FCSTD DOCUMENT  (FreeCAD 1.0RUnknown)
Label: wardrobe_jan
License: All rights reserved
LicenseURL: https://en.wikipedia.org/wiki/All_rights_reserved
objects: App::Link×45, App::FeaturePython×9, Measure::MeasureDistance×9, Assembly::AssemblyLink×5, Assembly::JointGroup×1, Assembly::AssemblyObject×1, App::DocumentObjectGroup×1
EXTERNAL_REF file=room_corner_chimney_left.FCStd obj=Body010
EXTERNAL_REF file=subassemblies/wardrobe_corpus00_jan.FCStd obj=Assembly
EXTERNAL_REF file=subassemblies/wardrobe_corpus00_jan.FCStd obj=wardrobe_base_jan
EXTERNAL_REF file=subassemblies/wardrobe_corpus00_jan.FCStd obj=wardrobe_right_jan_corpus00
EXTERNAL_REF file=subassemblies/wardrobe_corpus00_jan.FCStd obj=wardrobe_left_jan_corpus00
EXTERNAL_REF file=subassemblies/wardrobe_corpus00_jan.FCStd obj=wardrobe_top_jan
EXTERNAL_REF file=subassemblies/wardrobe_corpus00_jan.FCStd obj=wardrobe_backplate_jan_corpus00
EXTERNAL_REF file=subassemblies/wardrobe_corpus01_jan.FCStd obj=Assembly
EXTERNAL_REF file=subassemblies/wardrobe_corpus01_jan.FCStd obj=wardrobe_base_jan
EXTERNAL_REF file=subassemblies/wardrobe_corpus01_jan.FCStd obj=wardrobe_right_jan_corpus00
EXTERNAL_REF file=subassemblies/wardrobe_corpus01_jan.FCStd obj=wardrobe_left_jan_corpus00
EXTERNAL_REF file=subassemblies/wardrobe_corpus01_jan.FCStd obj=wardrobe_top_jan
EXTERNAL_REF file=subassemblies/wardrobe_corpus01_jan.FCStd obj=wardrobe_backplate_jan_corpus00
EXTERNAL_REF file=subassemblies/wardrobe_corpus02_jan.FCStd obj=Assembly
EXTERNAL_REF file=subassemblies/wardrobe_corpus02_jan.FCStd obj=wardrobe_base_jan
EXTERNAL_REF file=subassemblies/wardrobe_corpus02_jan.FCStd obj=wardrobe_right_jan_corpus00
EXTERNAL_REF file=subassemblies/wardrobe_corpus02_jan.FCStd obj=wardrobe_left_jan_corpus00
EXTERNAL_REF file=subassemblies/wardrobe_corpus02_jan.FCStd obj=wardrobe_top_jan
EXTERNAL_REF file=subassemblies/wardrobe_corpus02_jan.FCStd obj=wardrobe_backplate_jan_corpus00
EXTERNAL_REF file=subassemblies/wardrobe_corpus00_jan.FCStd obj=hettich_level_adjustment
EXTERNAL_REF file=subassemblies/wardrobe_corpus00_jan.FCStd obj=hettich_level_adjustment001
EXTERNAL_REF file=subassemblies/wardrobe_corpus00_jan.FCStd obj=hettich_level_adjustment002
EXTERNAL_REF file=subassemblies/wardrobe_corpus00_jan.FCStd obj=hettich_level_adjustment003
EXTERNAL_REF file=subassemblies/wardrobe_corpus01_jan.FCStd obj=hettich_level_adjustment
EXTERNAL_REF file=subassemblies/wardrobe_corpus01_jan.FCStd obj=hettich_level_adjustment001
EXTERNAL_REF file=subassemblies/wardrobe_corpus01_jan.FCStd obj=hettich_level_adjustment002
EXTERNAL_REF file=subassemblies/wardrobe_corpus01_jan.FCStd obj=hettich_level_adjustment003
EXTERNAL_REF file=subassemblies/wardrobe_corpus02_jan.FCStd obj=hettich_level_adjustment
EXTERNAL_REF file=subassemblies/wardrobe_corpus02_jan.FCStd obj=hettich_level_adjustment001
EXTERNAL_REF file=subassemblies/wardrobe_corpus02_jan.FCStd obj=hettich_level_adjustment002
EXTERNAL_REF file=subassemblies/wardrobe_corpus02_jan.FCStd obj=hettich_level_adjustment003
EXTERNAL_REF file=subassemblies/wardrobe_corpus00_jan.FCStd obj=wardrobe_door_corpus00_jan
EXTERNAL_REF file=subassemblies/wardrobe_corpus01_jan.FCStd obj=wardrobe_door_corpus01_jan
EXTERNAL_REF file=subassemblies/wardrobe_corpus02_jan.FCStd obj=wardrobe_door_corpus02_jan
EXTERNAL_REF file=subassemblies/wardrobe_drawer_jan.FCStd obj=Assembly
EXTERNAL_REF file=subassemblies/wardrobe_drawer_jan.FCStd obj=hettich_rail_550
EXTERNAL_REF file=subassemblies/wardrobe_drawer_jan.FCStd obj=hettich_rail_551
EXTERNAL_REF file=subassemblies/wardrobe_drawer_jan.FCStd obj=drawer_sides
EXTERNAL_REF file=subassemblies/wardrobe_drawer_jan.FCStd obj=drawer_sides001
EXTERNAL_REF file=subassemblies/wardrobe_drawer_jan.FCStd obj=drawer_back
EXTERNAL_REF file=subassemblies/wardrobe_drawer_jan.FCStd obj=drawer_bottom
EXTERNAL_REF file=subassemblies/wardrobe_drawer_jan.FCStd obj=drawer_front
EXTERNAL_REF file=subassemblies/wardrobe_corpus00_jan.FCStd obj=wardrobe_drawer_jan

FEATURE [App::Link] wall  label="wall001"
  LinkPlacement = pos=(267.099,327.988,3.33374) rot=(0,0,1;0rad)
  LinkedObject = -> <external room_corner_chimney_left.FCStd>#Body010
  Placement = pos=(267.099,327.988,3.33374) rot=(0,0,1;0rad)
FEATURE [App::FeaturePython] GroundedJoint  # Assembly grounded joint (typed FeaturePython)
  ObjectToGround = -> wall
  Placement = pos=(267.099,327.988,3.33374) rot=(0,0,1;0rad)
FEATURE [App::Link] wardrobe_base_jan
  LinkedObject = -> <external subassemblies/wardrobe_corpus00_jan.FCStd>#wardrobe_base_jan
FEATURE [App::Link] wardrobe_right_jan_corpus00  label="wardrobe_right_corpus00_jan"
  LinkPlacement = pos=(251,2.07e-13,1022.5) rot=(0,0,1;0rad)
  LinkedObject = -> <external subassemblies/wardrobe_corpus00_jan.FCStd>#wardrobe_right_jan_corpus00
  Placement = pos=(251,2.07e-13,1022.5) rot=(0,0,1;0rad)
FEATURE [App::Link] wardrobe_left_jan_corpus00  label="wardrobe_left_corpus00_jan"
  LinkPlacement = pos=(-270,2.1e-13,1022.5) rot=(0,0,1;0rad)
  LinkedObject = -> <external subassemblies/wardrobe_corpus00_jan.FCStd>#wardrobe_left_jan_corpus00
  Placement = pos=(-270,2.1e-13,1022.5) rot=(0,0,1;0rad)
FEATURE [App::Link] wardrobe_top_jan
  LinkPlacement = pos=(-6.835e-13,3.905e-13,2026) rot=(0,0,1;0rad)
  LinkedObject = -> <external subassemblies/wardrobe_corpus00_jan.FCStd>#wardrobe_top_jan
  Placement = pos=(-6.835e-13,3.905e-13,2026) rot=(0,0,1;0rad)
FEATURE [App::Link] wardrobe_backplate_jan_corpus00  label="wardrobe_backplate_corpus00_jan"
  LinkPlacement = pos=(-3e-15,300,1022.5) rot=(0,0,1;3.14159rad)
  LinkedObject = -> <external subassemblies/wardrobe_corpus00_jan.FCStd>#wardrobe_backplate_jan_corpus00
  Placement = pos=(-3e-15,300,1022.5) rot=(0,0,1;3.14159rad)
FEATURE [App::Link] wardrobe_base_jan001
  LinkedObject = -> <external subassemblies/wardrobe_corpus01_jan.FCStd>#wardrobe_base_jan
FEATURE [App::Link] wardrobe_right_jan_corpus001  label="wardrobe_right_corpus01_jan"
  LinkPlacement = pos=(251,1.01e-13,707.5) rot=(0,0,1;0rad)
  LinkedObject = -> <external subassemblies/wardrobe_corpus01_jan.FCStd>#wardrobe_right_jan_corpus00
  Placement = pos=(251,1.01e-13,707.5) rot=(0,0,1;0rad)
FEATURE [App::Link] wardrobe_left_jan_corpus001  label="wardrobe_left_corpus01_jan"
  LinkPlacement = pos=(-270,9.63e-14,707.5) rot=(0,0,1;0rad)
  LinkedObject = -> <external subassemblies/wardrobe_corpus01_jan.FCStd>#wardrobe_left_jan_corpus00
  Placement = pos=(-270,9.63e-14,707.5) rot=(0,0,1;0rad)
FEATURE [App::Link] wardrobe_top_jan001
  LinkPlacement = pos=(-4.699e-13,1.441e-13,1396) rot=(0,0,1;0rad)
  LinkedObject = -> <external subassemblies/wardrobe_corpus01_jan.FCStd>#wardrobe_top_jan
  Placement = pos=(-4.699e-13,1.441e-13,1396) rot=(0,0,1;0rad)
FEATURE [App::Link] wardrobe_backplate_jan_corpus001  label="wardrobe_backplate_corpus01_jan"
  LinkPlacement = pos=(-3e-15,300,707.5) rot=(0,0,1;3.14159rad)
  LinkedObject = -> <external subassemblies/wardrobe_corpus01_jan.FCStd>#wardrobe_backplate_jan_corpus00
  Placement = pos=(-3e-15,300,707.5) rot=(0,0,1;3.14159rad)
FEATURE [App::Link] wardrobe_base_jan002
  LinkedObject = -> <external subassemblies/wardrobe_corpus02_jan.FCStd>#wardrobe_base_jan
FEATURE [App::Link] wardrobe_right_jan_corpus002  label="wardrobe_right_corpus02_jan"
  LinkPlacement = pos=(251,-5.11e-14,390) rot=(0,0,1;0rad)
  LinkedObject = -> <external subassemblies/wardrobe_corpus02_jan.FCStd>#wardrobe_right_jan_corpus00
  Placement = pos=(251,-5.11e-14,390) rot=(0,0,1;0rad)
FEATURE [App::Link] wardrobe_left_jan_corpus002  label="wardrobe_left_corpus02_jan"
  LinkPlacement = pos=(-270,9.63e-14,390) rot=(0,0,1;0rad)
  LinkedObject = -> <external subassemblies/wardrobe_corpus02_jan.FCStd>#wardrobe_left_jan_corpus00
  Placement = pos=(-270,9.63e-14,390) rot=(0,0,1;0rad)
FEATURE [App::Link] wardrobe_top_jan002
  LinkPlacement = pos=(-2.095e-13,-1.636e-13,761) rot=(0,0,1;0rad)
  LinkedObject = -> <external subassemblies/wardrobe_corpus02_jan.FCStd>#wardrobe_top_jan
  Placement = pos=(-2.095e-13,-1.636e-13,761) rot=(0,0,1;0rad)
FEATURE [App::Link] wardrobe_backplate_jan_corpus002  label="wardrobe_backplate_corpus02_jan"
  LinkPlacement = pos=(-3e-15,300,390) rot=(0,0,1;3.14159rad)
  LinkedObject = -> <external subassemblies/wardrobe_corpus02_jan.FCStd>#wardrobe_backplate_jan_corpus00
  Placement = pos=(-3e-15,300,390) rot=(0,0,1;3.14159rad)
FEATURE [App::FeaturePython] Joint  label="Parallel"  # Assembly joint (typed FeaturePython)
  Activated = true
  AngleMax = 0
  AngleMin = 0
  Detach1 = false
  Detach2 = false
  Distance = 0
  Distance2 = 0
  EnableAngleMax = false
  EnableAngleMin = false
  EnableLengthMax = false
  EnableLengthMin = false
  JointType = 6 (Parallel)
  LengthMax = 0
  LengthMin = 0
  Placement1 = pos=(-1.2e-15,-19,0) rot=(-0.57735,-0.57735,-0.57735;2.0944rad)
  Placement2 = pos=(-777.564,-2.274e-13,902.667) rot=(-0.57735,-0.57735,-0.57735;2.0944rad)
  Reference1 = -> Assembly [wardrobe_corpus00_jan.wardrobe_backplate_jan_corpus00.Face6,wardrobe_corpus00_jan.wardrobe_backplate_jan_corpus00.Face6]
  Reference2 = -> Assembly [wall.Face7,wall.Face7]
FEATURE [App::FeaturePython] Joint001  label="Parallel001"  # Assembly joint (typed FeaturePython)
  Activated = true
  AngleMax = 0
  AngleMin = 0
  Detach1 = false
  Detach2 = false
  Distance = 0
  Distance2 = 0
  EnableAngleMax = false
  EnableAngleMin = false
  EnableLengthMax = false
  EnableLengthMin = false
  JointType = 6 (Parallel)
  LengthMax = 0
  LengthMin = 0
  Placement1 = pos=(19,1.005e-13,0) rot=(0.707107,0,0.707107;3.14159rad)
  Placement2 = pos=(0,-335,1240) rot=(0,-1,0;1.5708rad)
  Reference1 = -> Assembly [wardrobe_corpus00_jan.wardrobe_right_jan_corpus00.Face6,wardrobe_corpus00_jan.wardrobe_right_jan_corpus00.Face6]
  Reference2 = -> Assembly [wall.Face6,wall.Face6]
FEATURE [App::FeaturePython] Joint002  label="Parallel002"  # Assembly joint (typed FeaturePython)
  Activated = true
  AngleMax = 0
  AngleMin = 0
  Detach1 = false
  Detach2 = false
  Distance = 0
  Distance2 = 0
  EnableAngleMax = false
  EnableAngleMin = false
  EnableLengthMax = false
  EnableLengthMin = false
  JointType = 6 (Parallel)
  LengthMax = 0
  LengthMin = 0
  Placement1 = pos=(-1.3e-15,0,0) rot=(0,0,1;0rad)
  Placement2 = pos=(-1080,-335,7.37e-14) rot=(0,1,0;3.14159rad)
  Reference1 = -> Assembly [wardrobe_corpus00_jan.wardrobe_base_jan.Face5,wardrobe_corpus00_jan.wardrobe_base_jan.Face5]
  Reference2 = -> Assembly [wall.Face2,wall.Face2]
FEATURE [App::FeaturePython] Joint003  label="Abstand"  # Assembly joint (typed FeaturePython)
  Activated = true
  AngleMax = 0
  AngleMin = 0
  Detach1 = false
  Detach2 = false
  Distance = -30
  Distance2 = 0
  EnableAngleMax = false
  EnableAngleMin = false
  EnableLengthMax = false
  EnableLengthMin = false
  JointType = 5 (Distance)
  LengthMax = 0
  LengthMin = 0
  Placement1 = pos=(-1.3e-15,0,0) rot=(0,0,1;0rad)
  Placement2 = pos=(-1080,-335,7.37e-14) rot=(0,1,0;3.14159rad)
  Reference1 = -> Assembly [wardrobe_corpus00_jan.wardrobe_base_jan.Face5,wardrobe_corpus00_jan.wardrobe_base_jan.Face5]
  Reference2 = -> Assembly [wall.Face2,wall.Face2]
FEATURE [App::FeaturePython] Joint004  label="Abstand001"  # Assembly joint (typed FeaturePython)
  Activated = true
  AngleMax = 0
  AngleMin = 0
  Detach1 = false
  Detach2 = false
  Distance = 10
  Distance2 = 0
  EnableAngleMax = false
  EnableAngleMin = false
  EnableLengthMax = false
  EnableLengthMin = false
  JointType = 5 (Distance)
  LengthMax = 0
  LengthMin = 0
  Placement1 = pos=(19,1.005e-13,0) rot=(0.707107,0,0.707107;3.14159rad)
  Placement2 = pos=(0,-335,1240) rot=(0,-1,0;1.5708rad)
  Reference1 = -> Assembly [wardrobe_corpus00_jan.wardrobe_right_jan_corpus00.Face6,wardrobe_corpus00_jan.wardrobe_right_jan_corpus00.Face6]
  Reference2 = -> Assembly [wall.Face6,wall.Face6]
FEATURE [App::FeaturePython] Joint005  label="Abstand002"  # Assembly joint (typed FeaturePython)
  Activated = true
  AngleMax = 0
  AngleMin = 0
  Detach1 = false
  Detach2 = false
  Distance = 5
  Distance2 = 0
  EnableAngleMax = false
  EnableAngleMin = false
  EnableLengthMax = false
  EnableLengthMin = false
  JointType = 5 (Distance)
  LengthMax = 0
  LengthMin = 0
  Placement1 = pos=(-1.2e-15,-19,0) rot=(-0.57735,-0.57735,-0.57735;2.0944rad)
  Placement2 = pos=(-777.564,-2.274e-13,902.667) rot=(-0.57735,-0.57735,-0.57735;2.0944rad)
  Reference1 = -> Assembly [wardrobe_corpus00_jan.wardrobe_backplate_jan_corpus00.Face6,wardrobe_corpus00_jan.wardrobe_backplate_jan_corpus00.Face6]
  Reference2 = -> Assembly [wall.Face7,wall.Vertex11]
FEATURE [App::FeaturePython] Joint006  label="StarrerVerbund"  # Assembly joint (typed FeaturePython)
  Activated = true
  AngleMax = 0
  AngleMin = 0
  Detach1 = false
  Detach2 = false
  Distance = 0
  Distance2 = 0
  EnableAngleMax = false
  EnableAngleMin = false
  EnableLengthMax = false
  EnableLengthMin = false
  JointType = 0 (Fixed)
  LengthMax = 0
  LengthMin = 0
  Offset2 = pos=(0,0,0) rot=(0,0,1;3.14159rad)
  Placement1 = pos=(270,0,0) rot=(0.57735,0.57735,0.57735;4.18879rad)
  Placement2 = pos=(-270,0,0) rot=(-0.57735,0.57735,-0.57735;4.18879rad)
  Reference1 = -> Assembly [wardrobe_corpus01_jan.wardrobe_base_jan001.Edge6,wardrobe_corpus01_jan.wardrobe_base_jan001.Edge6]
  Reference2 = -> Assembly [wardrobe_corpus00_jan.wardrobe_base_jan.Edge11,wardrobe_corpus00_jan.wardrobe_base_jan.Edge11]
FEATURE [App::FeaturePython] Joint007  label="StarrerVerbund001"  # Assembly joint (typed FeaturePython)
  Activated = true
  AngleMax = 0
  AngleMin = 0
  Detach1 = false
  Detach2 = false
  Distance = 0
  Distance2 = 0
  EnableAngleMax = false
  EnableAngleMin = false
  EnableLengthMax = false
  EnableLengthMin = false
  JointType = 0 (Fixed)
  LengthMax = 0
  LengthMin = 0
  Offset2 = pos=(0,0,0) rot=(0,0,1;3.14159rad)
  Placement1 = pos=(270,0,0) rot=(0.57735,0.57735,0.57735;4.18879rad)
  Placement2 = pos=(-270,0,0) rot=(-0.57735,0.57735,-0.57735;4.18879rad)
  Reference1 = -> Assembly [wardrobe_corpus02_jan.wardrobe_base_jan002.Edge6,wardrobe_corpus02_jan.wardrobe_base_jan002.Edge6]
  Reference2 = -> Assembly [wardrobe_corpus01_jan.wardrobe_base_jan001.Edge11,wardrobe_corpus01_jan.wardrobe_base_jan001.Edge11]
FEATURE [Assembly::JointGroup] Joints
  Group = -> [GroundedJoint,Joint,Joint001,Joint002,Joint003,Joint004,Joint005,Joint006,Joint007]
FEATURE [App::Link] hettich_level_adjustment  label="hettich-level-adjustment"
  LinkPlacement = pos=(-218.25,-240,-1.33e-14) rot=(0.707107,-0.707107,0;3.14159rad)
  LinkedObject = -> <external subassemblies/wardrobe_corpus00_jan.FCStd>#hettich_level_adjustment
  Placement = pos=(-218.25,-240,-1.33e-14) rot=(0.707107,-0.707107,0;3.14159rad)
FEATURE [App::Link] hettich_level_adjustment001  label="hettich-level-adjustment001"
  LinkPlacement = pos=(218.25,-240,-3.9e-15) rot=(0.707107,-0.707107,0;3.14159rad)
  LinkedObject = -> <external subassemblies/wardrobe_corpus00_jan.FCStd>#hettich_level_adjustment001
  Placement = pos=(218.25,-240,-3.9e-15) rot=(0.707107,-0.707107,0;3.14159rad)
FEATURE [App::Link] hettich_level_adjustment002  label="hettich-level-adjustment002"
  LinkPlacement = pos=(218.25,240,-1.33e-14) rot=(0.707107,-0.707107,0;3.14159rad)
  LinkedObject = -> <external subassemblies/wardrobe_corpus00_jan.FCStd>#hettich_level_adjustment002
  Placement = pos=(218.25,240,-1.33e-14) rot=(0.707107,-0.707107,0;3.14159rad)
FEATURE [App::Link] hettich_level_adjustment003  label="hettich-level-adjustment003"
  LinkPlacement = pos=(-218.25,240,1.33e-14) rot=(0.707107,0.707107,0;3.14159rad)
  LinkedObject = -> <external subassemblies/wardrobe_corpus00_jan.FCStd>#hettich_level_adjustment003
  Placement = pos=(-218.25,240,1.33e-14) rot=(0.707107,0.707107,0;3.14159rad)
FEATURE [App::Link] hettich_level_adjustment004  label="hettich-level-adjustment004"
  LinkPlacement = pos=(-218.25,-240,-1.33e-14) rot=(0.707107,0.707107,0;3.14159rad)
  LinkedObject = -> <external subassemblies/wardrobe_corpus01_jan.FCStd>#hettich_level_adjustment
  Placement = pos=(-218.25,-240,-1.33e-14) rot=(0.707107,0.707107,0;3.14159rad)
FEATURE [App::Link] hettich_level_adjustment005  label="hettich-level-adjustment005"
  LinkPlacement = pos=(218.25,-240,1.33e-14) rot=(0.707107,-0.707107,0;3.14159rad)
  LinkedObject = -> <external subassemblies/wardrobe_corpus01_jan.FCStd>#hettich_level_adjustment001
  Placement = pos=(218.25,-240,1.33e-14) rot=(0.707107,-0.707107,0;3.14159rad)
FEATURE [App::Link] hettich_level_adjustment006  label="hettich-level-adjustment006"
  LinkPlacement = pos=(218.25,240,-1.33e-14) rot=(0.707107,-0.707107,0;3.14159rad)
  LinkedObject = -> <external subassemblies/wardrobe_corpus01_jan.FCStd>#hettich_level_adjustment002
  Placement = pos=(218.25,240,-1.33e-14) rot=(0.707107,-0.707107,0;3.14159rad)
FEATURE [App::Link] hettich_level_adjustment007  label="hettich-level-adjustment007"
  LinkPlacement = pos=(-218.25,240,1.33e-14) rot=(0.707107,0.707107,0;3.14159rad)
  LinkedObject = -> <external subassemblies/wardrobe_corpus01_jan.FCStd>#hettich_level_adjustment003
  Placement = pos=(-218.25,240,1.33e-14) rot=(0.707107,0.707107,0;3.14159rad)
FEATURE [App::Link] hettich_level_adjustment008  label="hettich-level-adjustment008"
  LinkPlacement = pos=(-218.25,-240,-1.33e-14) rot=(0.707107,0.707107,0;3.14159rad)
  LinkedObject = -> <external subassemblies/wardrobe_corpus02_jan.FCStd>#hettich_level_adjustment
  Placement = pos=(-218.25,-240,-1.33e-14) rot=(0.707107,0.707107,0;3.14159rad)
FEATURE [App::Link] hettich_level_adjustment009  label="hettich-level-adjustment009"
  LinkPlacement = pos=(218.25,-240,-3.9e-15) rot=(-0.707107,0.707107,0;3.14159rad)
  LinkedObject = -> <external subassemblies/wardrobe_corpus02_jan.FCStd>#hettich_level_adjustment001
  Placement = pos=(218.25,-240,-3.9e-15) rot=(-0.707107,0.707107,0;3.14159rad)
FEATURE [App::Link] hettich_level_adjustment010  label="hettich-level-adjustment010"
  LinkPlacement = pos=(218.25,240,-1.97e-14) rot=(0.707107,-0.707107,0;3.14159rad)
  LinkedObject = -> <external subassemblies/wardrobe_corpus02_jan.FCStd>#hettich_level_adjustment002
  Placement = pos=(218.25,240,-1.97e-14) rot=(0.707107,-0.707107,0;3.14159rad)
FEATURE [App::Link] hettich_level_adjustment011  label="hettich-level-adjustment011"
  LinkPlacement = pos=(-218.25,240,1.33e-14) rot=(0.707107,0.707107,0;3.14159rad)
  LinkedObject = -> <external subassemblies/wardrobe_corpus02_jan.FCStd>#hettich_level_adjustment003
  Placement = pos=(-218.25,240,1.33e-14) rot=(0.707107,0.707107,0;3.14159rad)
FEATURE [App::Link] wardrobe_door_corpus00_jan
  LinkPlacement = pos=(270,-302,2.5) rot=(0.57735,0.57735,0.57735;2.0944rad)
  LinkedObject = -> <external subassemblies/wardrobe_corpus00_jan.FCStd>#wardrobe_door_corpus00_jan
  Placement = pos=(270,-302,2.5) rot=(0.57735,0.57735,0.57735;2.0944rad)
FEATURE [App::Link] wardrobe_door_corpus01_jan
  LinkPlacement = pos=(267.5,-300,-2.1e-15) rot=(1,0,0;1.5708rad)
  LinkedObject = -> <external subassemblies/wardrobe_corpus01_jan.FCStd>#wardrobe_door_corpus01_jan
  Placement = pos=(267.5,-300,-2.1e-15) rot=(1,0,0;1.5708rad)
FEATURE [Assembly::AssemblyLink] wardrobe_corpus01_jan
  Group = -> [wardrobe_base_jan001,wardrobe_right_jan_corpus001,wardrobe_left_jan_corpus001,wardrobe_top_jan001,wardrobe_backplate_jan_corpus001,hettich_level_adjustment004,hettich_level_adjustment005,hettich_level_adjustment006,hettich_level_adjustment007,wardrobe_door_corpus01_jan]
  LinkedObject = -> <external subassemblies/wardrobe_corpus01_jan.FCStd>#Assembly
  Origin = -> Origin014
  Placement = pos=(-552.901,13.9879,33.3337) rot=(0,0,1;0rad)
  Rigid = true
FEATURE [App::Link] wardrobe_door_corpus02_jan
  LinkPlacement = pos=(267.5,-300,2.1e-15) rot=(1,0,0;1.5708rad)
  LinkedObject = -> <external subassemblies/wardrobe_corpus02_jan.FCStd>#wardrobe_door_corpus02_jan
  Placement = pos=(267.5,-300,2.1e-15) rot=(1,0,0;1.5708rad)
FEATURE [Assembly::AssemblyLink] wardrobe_corpus02_jan
  Group = -> [wardrobe_base_jan002,wardrobe_right_jan_corpus002,wardrobe_left_jan_corpus002,wardrobe_top_jan002,wardrobe_backplate_jan_corpus002,hettich_level_adjustment008,hettich_level_adjustment009,hettich_level_adjustment010,hettich_level_adjustment011,wardrobe_door_corpus02_jan]
  LinkedObject = -> <external subassemblies/wardrobe_corpus02_jan.FCStd>#Assembly
  Origin = -> Origin015
  Placement = pos=(-1092.9,13.9879,33.3337) rot=(0,0,1;0rad)
  Rigid = true
FEATURE [App::Link] hettich_rail_550
  LinkPlacement = pos=(0,-8.67788e-07,0) rot=(0.57735,0.57735,0.57735;2.0944rad)
  LinkedObject = -> <external subassemblies/wardrobe_drawer_jan.FCStd>#hettich_rail_550
  Placement = pos=(0,-8.67788e-07,0) rot=(0.57735,0.57735,0.57735;2.0944rad)
FEATURE [App::Link] hettich_rail_551  label="hettich_rail_550_1"
  LinkPlacement = pos=(502,3.32992e-05,-3.4167e-05) rot=(0.57735,-0.57735,-0.57735;2.0944rad)
  LinkedObject = -> <external subassemblies/wardrobe_drawer_jan.FCStd>#hettich_rail_551
  Placement = pos=(502,3.32992e-05,-3.4167e-05) rot=(0.57735,-0.57735,-0.57735;2.0944rad)
FEATURE [App::Link] drawer_sides
  LinkPlacement = pos=(22,256,72.5) rot=(-0.340731,0.659269,0.659269;0rad)
  LinkedObject = -> <external subassemblies/wardrobe_drawer_jan.FCStd>#drawer_sides
  Placement = pos=(22,256,72.5) rot=(-0.340731,0.659269,0.659269;0rad)
FEATURE [App::Link] drawer_sides001
  LinkPlacement = pos=(480,-256,72.5) rot=(0,0,1;3.14159rad)
  LinkedObject = -> <external subassemblies/wardrobe_drawer_jan.FCStd>#drawer_sides001
  Placement = pos=(480,-256,72.5) rot=(0,0,1;3.14159rad)
FEATURE [App::Link] drawer_back
  LinkPlacement = pos=(489.5,265.5,80.75) rot=(0,0,-1;1.5708rad)
  LinkedObject = -> <external subassemblies/wardrobe_drawer_jan.FCStd>#drawer_back
  Placement = pos=(489.5,265.5,80.75) rot=(0,0,-1;1.5708rad)
FEATURE [App::Link] drawer_bottom
  LinkPlacement = pos=(251,5.75002,-2.50002) rot=(0,0,1;3.14159rad)
  LinkedObject = -> <external subassemblies/wardrobe_drawer_jan.FCStd>#drawer_bottom
  Placement = pos=(251,5.75002,-2.50002) rot=(0,0,1;3.14159rad)
FEATURE [App::Link] drawer_front
  LinkPlacement = pos=(12.5,-265.5,72.5) rot=(0,0,1;1.5708rad)
  LinkedObject = -> <external subassemblies/wardrobe_drawer_jan.FCStd>#drawer_front
  Placement = pos=(12.5,-265.5,72.5) rot=(0,0,1;1.5708rad)
FEATURE [Assembly::AssemblyLink] wardrobe_drawer_jan
  Group = -> [hettich_rail_550,hettich_rail_551,drawer_sides,drawer_sides001,drawer_back,drawer_bottom,drawer_front]
  LinkedObject = -> <external subassemblies/wardrobe_drawer_jan.FCStd>#Assembly
  Placement = pos=(-251,8.67788e-07,36.5) rot=(0.340731,-0.659269,-0.659269;0rad)
  Rigid = true
FEATURE [App::Link] hettich_rail_552
  LinkPlacement = pos=(0,-8.67788e-07,0) rot=(0.57735,0.57735,0.57735;2.0944rad)
  LinkedObject = -> <external subassemblies/wardrobe_drawer_jan.FCStd>#hettich_rail_550
  Placement = pos=(0,-8.67788e-07,0) rot=(0.57735,0.57735,0.57735;2.0944rad)
FEATURE [App::Link] hettich_rail_553  label="hettich_rail_550_002"
  LinkPlacement = pos=(502,3.32992e-05,-3.4167e-05) rot=(0.57735,-0.57735,-0.57735;2.0944rad)
  LinkedObject = -> <external subassemblies/wardrobe_drawer_jan.FCStd>#hettich_rail_551
  Placement = pos=(502,3.32992e-05,-3.4167e-05) rot=(0.57735,-0.57735,-0.57735;2.0944rad)
FEATURE [App::Link] drawer_sides002
  LinkPlacement = pos=(22,256,72.5) rot=(-0.340731,0.659269,0.659269;0rad)
  LinkedObject = -> <external subassemblies/wardrobe_drawer_jan.FCStd>#drawer_sides
  Placement = pos=(22,256,72.5) rot=(-0.340731,0.659269,0.659269;0rad)
FEATURE [App::Link] drawer_sides003
  LinkPlacement = pos=(480,-256,72.5) rot=(0,0,1;3.14159rad)
  LinkedObject = -> <external subassemblies/wardrobe_drawer_jan.FCStd>#drawer_sides001
  Placement = pos=(480,-256,72.5) rot=(0,0,1;3.14159rad)
FEATURE [App::Link] drawer_back001
  LinkPlacement = pos=(489.5,265.5,80.75) rot=(0,0,-1;1.5708rad)
  LinkedObject = -> <external subassemblies/wardrobe_drawer_jan.FCStd>#drawer_back
  Placement = pos=(489.5,265.5,80.75) rot=(0,0,-1;1.5708rad)
FEATURE [App::Link] drawer_bottom001
  LinkPlacement = pos=(251,5.75002,-2.50002) rot=(0,0,1;3.14159rad)
  LinkedObject = -> <external subassemblies/wardrobe_drawer_jan.FCStd>#drawer_bottom
  Placement = pos=(251,5.75002,-2.50002) rot=(0,0,1;3.14159rad)
FEATURE [App::Link] drawer_front001
  LinkPlacement = pos=(12.5,-265.5,72.5) rot=(0,0,1;1.5708rad)
  LinkedObject = -> <external subassemblies/wardrobe_drawer_jan.FCStd>#drawer_front
  Placement = pos=(12.5,-265.5,72.5) rot=(0,0,1;1.5708rad)
FEATURE [Assembly::AssemblyLink] wardrobe_drawer_jan001
  Group = -> [hettich_rail_552,hettich_rail_553,drawer_sides002,drawer_sides003,drawer_back001,drawer_bottom001,drawer_front001]
  LinkedObject = -> <external subassemblies/wardrobe_corpus00_jan.FCStd>#wardrobe_drawer_jan
  Placement = pos=(-251,8.67788e-07,56.5) rot=(0.340731,-0.659269,-0.659269;0rad)
  Rigid = true
FEATURE [Assembly::AssemblyLink] wardrobe_corpus00_jan
  Group = -> [wardrobe_base_jan,wardrobe_right_jan_corpus00,wardrobe_left_jan_corpus00,wardrobe_top_jan,wardrobe_backplate_jan_corpus00,hettich_level_adjustment,hettich_level_adjustment001,hettich_level_adjustment002,hettich_level_adjustment003,wardrobe_door_corpus00_jan,wardrobe_drawer_jan,wardrobe_drawer_jan001]
  LinkedObject = -> <external subassemblies/wardrobe_corpus00_jan.FCStd>#Assembly
  Origin = -> Origin
  Placement = pos=(-12.9011,13.9879,33.3337) rot=(0,0,1;0rad)
  Rigid = true
FEATURE [Assembly::AssemblyObject] Assembly
  Group = -> [Joints,wall,GroundedJoint,wardrobe_corpus00_jan,wardrobe_corpus01_jan,wardrobe_corpus02_jan,Joint,Joint001,Joint002,Joint003,Joint004,Joint005,Joint006,Joint007]
  Origin = -> Origin003
  Type = Assembly
FEATURE [Measure::MeasureDistance] Distance  label="Distance: 12,26 mm"
  Distance = 12.257
  DistanceX = 9.31778
  DistanceY = 0
  DistanceZ = 7.96321
  Element1 = -> Assembly [wardrobe_corpus00_jan.wardrobe_top_jan.Pad003.Edge12]
  Element2 = -> Assembly [wall.Pad.Face4]
  Position1 = (-282.901,326.988,2078.33)
  Position2 = (-292.219,326.988,2086.3)
FEATURE [Measure::MeasureDistance] Distance001  label="Distance001: 11,05 mm"
  Distance = 11.0514
  DistanceX = 8.40128
  DistanceY = 0
  DistanceZ = 7.17995
  Element1 = -> Assembly [wardrobe_corpus01_jan.wardrobe_top_jan001.Pad003.Edge12]
  Element2 = -> Assembly [wall.Pad.Face4]
  Position1 = (-822.901,326.988,1448.33)
  Position2 = (-831.302,326.988,1455.51)
FEATURE [Measure::MeasureDistance] Distance002  label="Distance002: 13,09 mm"
  Distance = 13.0942
  DistanceX = 9.95424
  DistanceY = 0
  DistanceZ = 8.50715
  Element1 = -> Assembly [wardrobe_corpus02_jan.wardrobe_top_jan002.Pad003.Edge12]
  Element2 = -> Assembly [wall.Pad.Face4]
  Position1 = (-1362.9,326.988,813.334)
  Position2 = (-1372.86,326.988,821.841)
FEATURE [Measure::MeasureDistance] Distance003  label="Distance003: 2075,00 mm"
  Distance = 2075
  DistanceX = 0
  DistanceY = 4.547e-13
  DistanceZ = 2075
  Element1 = -> Assembly [wardrobe_corpus00_jan.wardrobe_top_jan.Pad003.Face6]
  Element2 = -> Assembly [wall.Pad.Face2]
  Position1 = (-282.901,-273.012,2078.33)
  Position2 = (-282.901,-273.012,3.33374)
FEATURE [Measure::MeasureDistance] Distance004  label="Distance004: 1445,00 mm"
  Distance = 1445
  DistanceX = 0
  DistanceY = 3.411e-13
  DistanceZ = 1445
  Element1 = -> Assembly [wardrobe_corpus01_jan.wardrobe_top_jan001.Pad003.Face6]
  Element2 = -> Assembly [wall.Pad.Face2]
  Position1 = (-822.901,-273.012,1448.33)
  Position2 = (-822.901,-273.012,3.33374)
FEATURE [Measure::MeasureDistance] Distance005  label="Distance005: 810,00 mm"
  Distance = 810
  DistanceX = 0
  DistanceY = 1.705e-13
  DistanceZ = 810
  Element1 = -> Assembly [wardrobe_corpus02_jan.wardrobe_top_jan002.Pad003.Face6]
  Element2 = -> Assembly [wall.Pad.Face2]
  Position1 = (-1362.9,-273.012,813.334)
  Position2 = (-1362.9,-273.012,3.33374)
FEATURE [Measure::MeasureDistance] Distance006  label="Distance006: 540,00 mm"
  Distance = 540
  DistanceX = 540
  DistanceY = 0
  DistanceZ = 0
  Element1 = -> Assembly [wardrobe_corpus00_jan.wardrobe_left_jan_corpus00.Pad001.Face5]
  Element2 = -> Assembly [wardrobe_corpus00_jan.wardrobe_right_jan_corpus00.Pad002.Face6]
  Position1 = (-282.901,-273.012,52.3337)
  Position2 = (257.099,-273.012,52.3337)
FEATURE [Measure::MeasureDistance] Distance007  label="Distance007: 10,00 mm"
  Distance = 10
  DistanceX = 10
  DistanceY = 0
  DistanceZ = 0
  Element1 = -> Assembly [wardrobe_corpus00_jan.wardrobe_right_jan_corpus00.Pad002.Face6]
  Element2 = -> Assembly [wall.Pad.Face6]
  Position1 = (257.099,-273.012,52.3337)
  Position2 = (267.099,-273.012,52.3337)
FEATURE [Measure::MeasureDistance] Distance008  label="Distance008: 30,00 mm"
  Distance = 30
  DistanceX = 0
  DistanceY = 0
  DistanceZ = 30
  Element1 = -> Assembly [wardrobe_corpus00_jan.wardrobe_base_jan.Pad.Face5]
  Element2 = -> Assembly [wall.Pad.Face2]
  Position1 = (-282.901,-273.012,33.3337)
  Position2 = (-282.901,-273.012,3.33374)
FEATURE [App::DocumentObjectGroup] Measurements
  Group = -> [Distance,Distance001,Distance002,Distance003,Distance004,Distance005,Distance006,Distance007,Distance008]

RESOLVED EXTERNAL PARTS (link-assembly join: the EXTERNAL_REF files above that resolve inside this repo's crawl, each included once):
---- part room_corner_chimney_left.FCStd = doc fcstd_721c1199e5e2 ----
FCSTD DOCUMENT  (FreeCAD 1.0RUnknown)
Label: room_corner_chimney_left
License: All rights reserved
LicenseURL: https://en.wikipedia.org/wiki/All_rights_reserved
objects: Sketcher::SketchObject×2, PartDesign::Pad×2, PartDesign::CoordinateSystem×2, PartDesign::Body×1
note: 13 computed .brp shape members not serialized (recipe doc carries the construction recipe); baked Part::Feature solids carry a one-line shape summary decoded from their .brp

FEATURE [Sketcher::SketchObject] Sketch010
  ArcFitTolerance = 1e-06
  AttachmentSupport = -> [XZ_Plane013]
  FullyConstrained = true
  MakeInternals = false
  MapMode = 5
  Placement = pos=(0,0,0) rot=(1,0,0;1.5708rad)
  sketch-geometry (10):
    g0: LineSegment StartX=0 StartY=0 StartZ=0 EndX=-2160 EndY=0 EndZ=0
    g1: LineSegment StartX=-2160 StartY=0 StartZ=0 EndX=-2160 EndY=210 EndZ=0
    g2: LineSegment StartX=0 StartY=0 StartZ=0 EndX=0 EndY=2480 EndZ=0
    g3: LineSegment StartX=0 StartY=2480 StartZ=0 EndX=-220 EndY=2480 EndZ=0
    g4: LineSegment StartX=-2160 StartY=210 StartZ=0 EndX=-220 EndY=2480 EndZ=0
    g5: LineSegment StartX=-2170 StartY=213.691 StartZ=0 EndX=-224.608 EndY=2490 EndZ=0
    g6: LineSegment StartX=10 StartY=2490 StartZ=0 EndX=-224.608 EndY=2490 EndZ=0
    g7: LineSegment StartX=10 StartY=-10 StartZ=0 EndX=10 EndY=2490 EndZ=0
    g8: LineSegment StartX=10 StartY=-10 StartZ=0 EndX=-2170 EndY=-10 EndZ=0
    g9: LineSegment StartX=-2170 StartY=-10 StartZ=0 EndX=-2170 EndY=213.691 EndZ=0
  constraints (23):
    c: Distance(g0) = 2160
    c: Coincident(g0,g-1)
    c: Horizontal(g0)
    c: Distance(g1) = 210
    c: Coincident(g1,g0)
    c: Vertical(g1)
    c: Distance(g2) = 2480
    c: Coincident(g2,g0)
    c: PointOnObject(g2,g-2)
    c: Distance(g3) = 220
    c: Coincident(g3,g2)
    c: Horizontal(g3)
    c: Coincident(g4,g1)
    c: Coincident(g4,g3)
    c: Coincident(g5,g6)
    c: Coincident(g5,g9)
    c: Coincident(g6,g7)
    c: Coincident(g7,g8)
    c: Coincident(g8,g9)
    c: Block(g5)
    c: Block(g6)
    c: Block(g7)
    c: Block(g8)
FEATURE [PartDesign::Pad] Pad010
  Direction = (0,-1,2e-16)
  Length = 670
  Length2 = 10
  Placement = pos=(0,0,0) rot=(1,0,0;1.5708rad)
  Profile = -> Sketch010
  ReferenceAxis = -> Sketch010 [N_Axis]
  Refine = true
  Suppressed = false
  Type = 0
FEATURE [Sketcher::SketchObject] Sketch
  ArcFitTolerance = 1e-06
  AttachmentSupport = -> [Pad010]
  ExternalGeometry = -> [Pad010]
  FullyConstrained = true
  MakeInternals = false
  MapMode = 5
  Placement = pos=(0,2.111e-13,0) rot=(-1,0,0;1.5708rad)
  sketch-geometry (5):
    g0: LineSegment StartX=10 StartY=-2490 StartZ=0 EndX=10 EndY=10 EndZ=0
    g1: LineSegment StartX=10 StartY=10 StartZ=0 EndX=-2170 EndY=10 EndZ=0
    g2: LineSegment StartX=-2170 StartY=10 StartZ=0 EndX=-2170 EndY=-213.691 EndZ=0
    g3: LineSegment StartX=-2170 StartY=-213.691 StartZ=0 EndX=-224.608 EndY=-2490 EndZ=0
    g4: LineSegment StartX=-224.608 StartY=-2490 StartZ=0 EndX=10 EndY=-2490 EndZ=0
  constraints (10):
    c: Coincident(g0,g-5)
    c: Coincident(g0,g-4)
    c: Coincident(g1,g0)
    c: Coincident(g1,g-7)
    c: Coincident(g2,g1)
    c: Coincident(g2,g-7)
    c: Coincident(g3,g2)
    c: Coincident(g3,g-6)
    c: Coincident(g4,g3)
    c: Coincident(g4,g0)
FEATURE [PartDesign::Pad] Pad
  BaseFeature = -> Pad010
  Direction = (0,1,2e-16)
  Length = 10
  Length2 = 10
  Placement = pos=(0,0,0) rot=(1,0,0;1.5708rad)
  Profile = -> Sketch
  ReferenceAxis = -> Sketch [N_Axis]
  Refine = true
  Suppressed = false
  Type = 0
FEATURE [PartDesign::CoordinateSystem] LCS_1
  AttacherType = Attacher::AttachEngine3D
  AttachmentSupport = -> [Pad]
  MapMode = 45
  Placement = pos=(-1080,-330,-10) rot=(0,0,1;1.5708rad)
FEATURE [PartDesign::CoordinateSystem] LCS_inner
  AttacherType = Attacher::AttachEngine3D
  AttachmentSupport = -> [Pad]
  MapMode = 7
  Placement = pos=(0,0,0) rot=(0,0.707107,0.707107;3.14159rad)
FEATURE [PartDesign::Body] Body010  label="wall"
  AllowCompound = false
  Group = -> [Sketch010,Pad010,Sketch,Pad,LCS_1,LCS_inner]
  Origin = -> Origin013
  Tip = -> Pad
---- part subassemblies/wardrobe_corpus00_jan.FCStd = doc fcstd_a64ae2e9aad0 ----
FCSTD DOCUMENT  (FreeCAD 1.0RUnknown)
Label: wardrobe_corpus00_jan
License: All rights reserved
LicenseURL: https://en.wikipedia.org/wiki/All_rights_reserved
objects: App::Link×17, App::FeaturePython×11, Assembly::AssemblyLink×1, Assembly::JointGroup×1, Assembly::AssemblyObject×1
EXTERNAL_REF file=parts/wardrobe_base_jan.FCStd obj=Body
EXTERNAL_REF file=parts/wardrobe_right_corpus00_jan.FCStd obj=Body002
EXTERNAL_REF file=parts/wardrobe_left_corpus00_jan.FCStd obj=Body001
EXTERNAL_REF file=parts/wardrobe_top_jan.FCStd obj=Body003
EXTERNAL_REF file=parts/wardrobe_backplate_corpus00_jan.FCStd obj=Body004
EXTERNAL_REF file=../purchased parts/hettich-level-adjustment.FCStd obj=Body
EXTERNAL_REF file=parts/wardrobe_door_corpus00_jan.FCStd obj=Body
EXTERNAL_REF file=wardrobe_drawer_jan.FCStd obj=Assembly
EXTERNAL_REF file=wardrobe_drawer_jan.FCStd obj=hettich_rail_550
EXTERNAL_REF file=wardrobe_drawer_jan.FCStd obj=hettich_rail_551
EXTERNAL_REF file=wardrobe_drawer_jan.FCStd obj=drawer_sides
EXTERNAL_REF file=wardrobe_drawer_jan.FCStd obj=drawer_sides001
EXTERNAL_REF file=wardrobe_drawer_jan.FCStd obj=drawer_back
EXTERNAL_REF file=wardrobe_drawer_jan.FCStd obj=drawer_bottom
EXTERNAL_REF file=wardrobe_drawer_jan.FCStd obj=drawer_front

FEATURE [App::Link] wardrobe_base_jan
  LinkedObject = -> <external parts/wardrobe_base_jan.FCStd>#Body
FEATURE [App::FeaturePython] GroundedJoint  # Assembly grounded joint (typed FeaturePython)
  ObjectToGround = -> wardrobe_base_jan
FEATURE [App::Link] wardrobe_right_jan_corpus00  label="wardrobe_right_corpus00_jan"
  LinkPlacement = pos=(251,2.07e-13,1022.5) rot=(0,0,1;0rad)
  LinkedObject = -> <external parts/wardrobe_right_corpus00_jan.FCStd>#Body002
  Placement = pos=(251,2.07e-13,1022.5) rot=(0,0,1;0rad)
FEATURE [App::Link] wardrobe_left_jan_corpus00  label="wardrobe_left_corpus00_jan"
  LinkPlacement = pos=(-270,2.1e-13,1022.5) rot=(0,0,1;0rad)
  LinkedObject = -> <external parts/wardrobe_left_corpus00_jan.FCStd>#Body001
  Placement = pos=(-270,2.1e-13,1022.5) rot=(0,0,1;0rad)
FEATURE [App::Link] wardrobe_top_jan
  LinkPlacement = pos=(-6.835e-13,3.905e-13,2026) rot=(0,0,1;0rad)
  LinkedObject = -> <external parts/wardrobe_top_jan.FCStd>#Body003
  Placement = pos=(-6.835e-13,3.905e-13,2026) rot=(0,0,1;0rad)
FEATURE [App::Link] wardrobe_backplate_jan_corpus00  label="wardrobe_backplate_corpus00_jan"
  LinkPlacement = pos=(-3e-15,300,1022.5) rot=(0,0,1;3.14159rad)
  LinkedObject = -> <external parts/wardrobe_backplate_corpus00_jan.FCStd>#Body004
  Placement = pos=(-3e-15,300,1022.5) rot=(0,0,1;3.14159rad)
FEATURE [App::FeaturePython] Joint002  label="StarrerVerbund002"  # Assembly joint (typed FeaturePython)
  Activated = true
  AngleMax = 0
  AngleMin = 0
  Detach1 = false
  Detach2 = false
  Distance = 0
  Distance2 = 0
  EnableAngleMax = false
  EnableAngleMin = false
  EnableLengthMax = false
  EnableLengthMin = false
  JointType = 0 (Fixed)
  LengthMax = 0
  LengthMin = 0
  Offset2 = pos=(0,0,0) rot=(0,0,1;3.14159rad)
  Placement1 = pos=(-3e-15,0,-1022.5) rot=(0.707107,0,0.707107;3.14159rad)
  Placement2 = pos=(0,300,0) rot=(0,1,0;4.71239rad)
  Reference1 = -> Assembly [wardrobe_backplate_jan_corpus00.Edge3,wardrobe_backplate_jan_corpus00.Edge3]
  Reference2 = -> Assembly [wardrobe_base_jan.Edge9,wardrobe_base_jan.Edge9]
FEATURE [App::FeaturePython] Joint  label="StarrerVerbund"  # Assembly joint (typed FeaturePython)
  Activated = true
  AngleMax = 0
  AngleMin = 0
  Detach1 = false
  Detach2 = false
  Distance = 0
  Distance2 = 0
  EnableAngleMax = false
  EnableAngleMin = false
  EnableLengthMax = false
  EnableLengthMin = false
  JointType = 0 (Fixed)
  LengthMax = 0
  LengthMin = 0
  Placement1 = pos=(19,-2.07e-13,-1003.5) rot=(0.57735,0.57735,0.57735;4.18879rad)
  Placement2 = pos=(270,0,19) rot=(0.57735,0.57735,0.57735;4.18879rad)
  Reference1 = -> Assembly [wardrobe_right_jan_corpus00.Edge4,wardrobe_right_jan_corpus00.Edge4]
  Reference2 = -> Assembly [wardrobe_base_jan.Edge7,wardrobe_base_jan.Edge7]
FEATURE [App::FeaturePython] Joint003  label="StarrerVerbund003"  # Assembly joint (typed FeaturePython)
  Activated = true
  AngleMax = 0
  AngleMin = 0
  Detach1 = false
  Detach2 = false
  Distance = 0
  Distance2 = 0
  EnableAngleMax = false
  EnableAngleMin = false
  EnableLengthMax = false
  EnableLengthMin = false
  JointType = 0 (Fixed)
  LengthMax = 0
  LengthMin = 0
  Offset2 = pos=(0,0,0) rot=(0,0,1;3.14159rad)
  Placement1 = pos=(3.411e-13,-2.1e-13,-1003.5) rot=(0.57735,0.57735,0.57735;4.18879rad)
  Placement2 = pos=(-270,0,19) rot=(-0.57735,0.57735,-0.57735;4.18879rad)
  Reference1 = -> Assembly [wardrobe_left_jan_corpus00.Edge3,wardrobe_left_jan_corpus00.Edge3]
  Reference2 = -> Assembly [wardrobe_base_jan.Edge12,wardrobe_base_jan.Edge12]
FEATURE [App::FeaturePython] Joint004  label="StarrerVerbund004"  # Assembly joint (typed FeaturePython)
  Activated = true
  AngleMax = 0
  AngleMin = 0
  Detach1 = false
  Detach2 = false
  Distance = 0
  Distance2 = 0
  EnableAngleMax = false
  EnableAngleMin = false
  EnableLengthMax = false
  EnableLengthMin = false
  JointType = 0 (Fixed)
  LengthMax = 0
  LengthMin = 0
  Offset2 = pos=(0,0,0) rot=(0,0,1;3.14159rad)
  Placement1 = pos=(270,4.3e-15,0) rot=(0.57735,0.57735,0.57735;4.18879rad)
  Placement2 = pos=(19,2.477e-13,1003.5) rot=(-0.57735,0.57735,-0.57735;4.18879rad)
  Reference1 = -> Assembly [wardrobe_top_jan.Edge6,wardrobe_top_jan.Edge6]
  Reference2 = -> Assembly [wardrobe_right_jan_corpus00.Edge10,wardrobe_right_jan_corpus00.Edge10]
FEATURE [App::Link] hettich_level_adjustment  label="hettich-level-adjustment"
  LinkPlacement = pos=(-218.25,-240,-1.33e-14) rot=(0.707107,-0.707107,0;3.14159rad)
  LinkedObject = -> <external ../purchased parts/hettich-level-adjustment.FCStd>#Body
  Placement = pos=(-218.25,-240,-1.33e-14) rot=(0.707107,-0.707107,0;3.14159rad)
FEATURE [App::FeaturePython] Joint005  label="StarrerVerbund005"  # Assembly joint (typed FeaturePython)
  Activated = true
  AngleMax = 0
  AngleMin = 0
  Detach1 = false
  Detach2 = false
  Distance = 0
  Distance2 = 0
  EnableAngleMax = false
  EnableAngleMin = false
  EnableLengthMax = false
  EnableLengthMin = false
  JointType = 0 (Fixed)
  LengthMax = 0
  LengthMin = 0
  Offset1 = pos=(0,-20,-60) rot=(0,0,1;0rad)
  Offset2 = pos=(0,0,0) rot=(0,0,1;3.14159rad)
  Placement1 = pos=(60,51.75,0) rot=(-0.707107,0,0.707107;3.14159rad)
  Placement2 = pos=(-270,-300,0) rot=(-0.57735,0.57735,-0.57735;4.18879rad)
  Reference1 = -> Assembly [hettich_level_adjustment.Edge25,hettich_level_adjustment.Edge25]
  Reference2 = -> Assembly [wardrobe_base_jan.Edge11,wardrobe_base_jan.Vertex1]
FEATURE [App::Link] hettich_level_adjustment001  label="hettich-level-adjustment001"
  LinkPlacement = pos=(218.25,-240,-3.9e-15) rot=(0.707107,-0.707107,0;3.14159rad)
  LinkedObject = -> <external ../purchased parts/hettich-level-adjustment.FCStd>#Body
  Placement = pos=(218.25,-240,-3.9e-15) rot=(0.707107,-0.707107,0;3.14159rad)
FEATURE [App::Link] hettich_level_adjustment002  label="hettich-level-adjustment002"
  LinkPlacement = pos=(218.25,240,-1.33e-14) rot=(0.707107,-0.707107,0;3.14159rad)
  LinkedObject = -> <external ../purchased parts/hettich-level-adjustment.FCStd>#Body
  Placement = pos=(218.25,240,-1.33e-14) rot=(0.707107,-0.707107,0;3.14159rad)
FEATURE [App::Link] hettich_level_adjustment003  label="hettich-level-adjustment003"
  LinkPlacement = pos=(-218.25,240,1.33e-14) rot=(0.707107,0.707107,0;3.14159rad)
  LinkedObject = -> <external ../purchased parts/hettich-level-adjustment.FCStd>#Body
  Placement = pos=(-218.25,240,1.33e-14) rot=(0.707107,0.707107,0;3.14159rad)
FEATURE [App::FeaturePython] Joint006  label="StarrerVerbund006"  # Assembly joint (typed FeaturePython)
  Activated = true
  AngleMax = 0
  AngleMin = 0
  Detach1 = false
  Detach2 = false
  Distance = 0
  Distance2 = 0
  EnableAngleMax = false
  EnableAngleMin = false
  EnableLengthMax = false
  EnableLengthMin = false
  JointType = 0 (Fixed)
  LengthMax = 0
  LengthMin = 0
  Offset1 = pos=(0,-20,60) rot=(0,0,1;0rad)
  Offset2 = pos=(0,0,0) rot=(0,0,1;3.14159rad)
  Placement1 = pos=(250,-240,0) rot=(0.57735,0.57735,0.57735;4.18879rad)
  Placement2 = pos=(0,-31.75,0) rot=(0,-1,0;4.71239rad)
  Reference1 = -> Assembly [wardrobe_base_jan.Edge6,wardrobe_base_jan.Vertex3]
  Reference2 = -> Assembly [hettich_level_adjustment001.Edge10,hettich_level_adjustment001.Edge10]
FEATURE [App::FeaturePython] Joint007  label="StarrerVerbund007"  # Assembly joint (typed FeaturePython)
  Activated = true
  AngleMax = 0
  AngleMin = 0
  Detach1 = false
  Detach2 = false
  Distance = 0
  Distance2 = 0
  EnableAngleMax = false
  EnableAngleMin = false
  EnableLengthMax = false
  EnableLengthMin = false
  JointType = 0 (Fixed)
  LengthMax = 0
  LengthMin = 0
  Offset1 = pos=(0,20,-60) rot=(0,0,1;0rad)
  Offset2 = pos=(0,0,0) rot=(0,0,1;3.14159rad)
  Placement1 = pos=(-60,-51.75,0) rot=(0.707107,0,0.707107;3.14159rad)
  Placement2 = pos=(270,300,0) rot=(0.57735,-0.57735,-0.57735;4.18879rad)
  Reference1 = -> Assembly [hettich_level_adjustment002.Edge10,hettich_level_adjustment002.Edge10]
  Reference2 = -> Assembly [wardrobe_base_jan.Edge6,wardrobe_base_jan.Vertex5]
FEATURE [App::FeaturePython] Joint008  label="StarrerVerbund008"  # Assembly joint (typed FeaturePython)
  Activated = true
  AngleMax = 0
  AngleMin = 0
  Detach1 = false
  Detach2 = false
  Distance = 0
  Distance2 = 0
  EnableAngleMax = false
  EnableAngleMin = false
  EnableLengthMax = false
  EnableLengthMin = false
  JointType = 0 (Fixed)
  LengthMax = 0
  LengthMin = 0
  Offset1 = pos=(0,20,60) rot=(0,0,1;0rad)
  Placement1 = pos=(60,-51.75,0) rot=(0.707107,0,0.707107;3.14159rad)
  Placement2 = pos=(-270,300,0) rot=(-0.57735,-0.57735,0.57735;4.18879rad)
  Reference1 = -> Assembly [hettich_level_adjustment003.Edge10,hettich_level_adjustment003.Edge10]
  Reference2 = -> Assembly [wardrobe_base_jan.Edge11,wardrobe_base_jan.Vertex7]
FEATURE [App::Link] wardrobe_door_corpus00_jan
  LinkPlacement = pos=(270,-302,2.5) rot=(0.57735,0.57735,0.57735;2.0944rad)
  LinkedObject = -> <external parts/wardrobe_door_corpus00_jan.FCStd>#Body
  Placement = pos=(270,-302,2.5) rot=(0.57735,0.57735,0.57735;2.0944rad)
FEATURE [App::FeaturePython] Joint009  label="Drehverbindung"  # Assembly joint (typed FeaturePython)
  Activated = true
  AngleMax = 90
  AngleMin = 0
  Detach1 = false
  Detach2 = false
  Distance = 0
  Distance2 = 0
  EnableAngleMax = true
  EnableAngleMin = true
  EnableLengthMax = false
  EnableLengthMin = false
  JointType = 1 (Revolute)
  LengthMax = 0
  LengthMin = 0
  Offset1 = pos=(0,2,0) rot=(0,0,1;0rad)
  Offset2 = pos=(0,0,2.5) rot=(0,0,1;0rad)
  Placement1 = pos=(2,0,0) rot=(0.57735,0.57735,0.57735;4.18879rad)
  Placement2 = pos=(270,-300,2.5) rot=(0,0,1;0rad)
  Reference1 = -> Assembly [wardrobe_door_corpus00_jan.Edge3,wardrobe_door_corpus00_jan.Vertex1]
  Reference2 = -> Assembly [wardrobe_base_jan.Edge2,wardrobe_base_jan.Vertex3]
FEATURE [App::Link] hettich_rail_550
  LinkPlacement = pos=(0,-8.67788e-07,0) rot=(0.57735,0.57735,0.57735;2.0944rad)
  LinkedObject = -> <external wardrobe_drawer_jan.FCStd>#hettich_rail_550
  Placement = pos=(0,-8.67788e-07,0) rot=(0.57735,0.57735,0.57735;2.0944rad)
FEATURE [App::Link] hettich_rail_551  label="hettich_rail_550_1"
  LinkPlacement = pos=(502,3.32992e-05,-3.4167e-05) rot=(0.57735,-0.57735,-0.57735;2.0944rad)
  LinkedObject = -> <external wardrobe_drawer_jan.FCStd>#hettich_rail_551
  Placement = pos=(502,3.32992e-05,-3.4167e-05) rot=(0.57735,-0.57735,-0.57735;2.0944rad)
FEATURE [App::Link] drawer_sides
  LinkPlacement = pos=(22,256,72.5) rot=(-0.340731,0.659269,0.659269;0rad)
  LinkedObject = -> <external wardrobe_drawer_jan.FCStd>#drawer_sides
  Placement = pos=(22,256,72.5) rot=(-0.340731,0.659269,0.659269;0rad)
FEATURE [App::Link] drawer_sides001
  LinkPlacement = pos=(480,-256,72.5) rot=(0,0,1;3.14159rad)
  LinkedObject = -> <external wardrobe_drawer_jan.FCStd>#drawer_sides001
  Placement = pos=(480,-256,72.5) rot=(0,0,1;3.14159rad)
FEATURE [App::Link] drawer_back
  LinkPlacement = pos=(489.5,265.5,80.75) rot=(0,0,-1;1.5708rad)
  LinkedObject = -> <external wardrobe_drawer_jan.FCStd>#drawer_back
  Placement = pos=(489.5,265.5,80.75) rot=(0,0,-1;1.5708rad)
FEATURE [App::Link] drawer_bottom
  LinkPlacement = pos=(251,5.75002,-2.50002) rot=(0,0,1;3.14159rad)
  LinkedObject = -> <external wardrobe_drawer_jan.FCStd>#drawer_bottom
  Placement = pos=(251,5.75002,-2.50002) rot=(0,0,1;3.14159rad)
FEATURE [App::Link] drawer_front
  LinkPlacement = pos=(12.5,-265.5,72.5) rot=(0,0,1;1.5708rad)
  LinkedObject = -> <external wardrobe_drawer_jan.FCStd>#drawer_front
  Placement = pos=(12.5,-265.5,72.5) rot=(0,0,1;1.5708rad)
FEATURE [Assembly::AssemblyLink] wardrobe_drawer_jan
  Group = -> [hettich_rail_550,hettich_rail_551,drawer_sides,drawer_sides001,drawer_back,drawer_bottom,drawer_front]
  LinkedObject = -> <external wardrobe_drawer_jan.FCStd>#Assembly
  Origin = -> Origin001
  Placement = pos=(-251,8.67788e-07,56.5) rot=(0.340731,-0.659269,-0.659269;0rad)
  Rigid = true
FEATURE [App::FeaturePython] Joint010  label="StarrerVerbund009"  # Assembly joint (typed FeaturePython)
  Activated = true
  AngleMax = 0
  AngleMin = 0
  Detach1 = false
  Detach2 = false
  Distance = 0
  Distance2 = 0
  EnableAngleMax = false
  EnableAngleMin = false
  EnableLengthMax = false
  EnableLengthMin = false
  JointType = 0 (Fixed)
  LengthMax = 0
  LengthMin = 0
  Offset1 = pos=(0,20,0) rot=(0,0,1;0rad)
  Offset2 = pos=(0,0,0) rot=(0,0,1;1.5708rad)
  Placement1 = pos=(-3.52e-14,-37.5,-1.6e-15) rot=(0.707107,0,0.707107;3.14159rad)
  Placement2 = pos=(19,-2.1e-13,-1003.5) rot=(1,0,0;4.71239rad)
  Reference1 = -> Assembly [wardrobe_drawer_jan.hettich_rail_550.Edge3,wardrobe_drawer_jan.hettich_rail_550.Edge3]
  Reference2 = -> Assembly [wardrobe_left_jan_corpus00.Edge4,wardrobe_left_jan_corpus00.Edge4]
FEATURE [Assembly::JointGroup] Joints
  Group = -> [GroundedJoint,Joint002,Joint,Joint003,Joint004,Joint005,Joint006,Joint007,Joint008,Joint009,Joint010]
FEATURE [Assembly::AssemblyObject] Assembly  label="wardrobe_corpus00_jan"
  Group = -> [Joints,wardrobe_base_jan,GroundedJoint,wardrobe_right_jan_corpus00,wardrobe_left_jan_corpus00,wardrobe_top_jan,wardrobe_backplate_jan_corpus00,Joint002,Joint,Joint003,Joint004,hettich_level_adjustment,Joint005,hettich_level_adjustment001,hettich_level_adjustment002,hettich_level_adjustment003,Joint006,Joint007,Joint008,wardrobe_door_corpus00_jan,Joint009,wardrobe_drawer_jan,Joint010]
  Origin = -> Origin
  Type = Assembly
---- part subassemblies/wardrobe_corpus01_jan.FCStd = doc fcstd_56d9dd2ddcd5 ----
FCSTD DOCUMENT  (FreeCAD 1.0RUnknown)
Label: wardrobe_corpus01_jan
License: All rights reserved
LicenseURL: https://en.wikipedia.org/wiki/All_rights_reserved
objects: App::FeaturePython×15, App::Link×10, Assembly::JointGroup×1, Assembly::AssemblyObject×1
EXTERNAL_REF file=parts/wardrobe_base_jan.FCStd obj=Body
EXTERNAL_REF file=parts/wardrobe_right_corpus01_jan.FCStd obj=Body002
EXTERNAL_REF file=parts/wardrobe_left_corpus01_jan.FCStd obj=Body001
EXTERNAL_REF file=parts/wardrobe_top_jan.FCStd obj=Body003
EXTERNAL_REF file=parts/wardrobe_backplate_corpus01_jan.FCStd obj=Body004
EXTERNAL_REF file=../purchased parts/hettich-level-adjustment.FCStd obj=Body
EXTERNAL_REF file=parts/wardrobe_door_corpus01_jan.FCStd obj=Body

FEATURE [App::Link] wardrobe_base_jan
  LinkedObject = -> <external parts/wardrobe_base_jan.FCStd>#Body
FEATURE [App::FeaturePython] GroundedJoint  # Assembly grounded joint (typed FeaturePython)
  ObjectToGround = -> wardrobe_base_jan
FEATURE [App::Link] wardrobe_right_jan_corpus00  label="wardrobe_right_corpus01_jan"
  LinkPlacement = pos=(251,1.01e-13,707.5) rot=(0,0,1;0rad)
  LinkedObject = -> <external parts/wardrobe_right_corpus01_jan.FCStd>#Body002
  Placement = pos=(251,1.01e-13,707.5) rot=(0,0,1;0rad)
FEATURE [App::Link] wardrobe_left_jan_corpus00  label="wardrobe_left_corpus01_jan"
  LinkPlacement = pos=(-270,9.63e-14,707.5) rot=(0,0,1;0rad)
  LinkedObject = -> <external parts/wardrobe_left_corpus01_jan.FCStd>#Body001
  Placement = pos=(-270,9.63e-14,707.5) rot=(0,0,1;0rad)
FEATURE [App::Link] wardrobe_top_jan
  LinkPlacement = pos=(-4.699e-13,1.441e-13,1396) rot=(0,0,1;0rad)
  LinkedObject = -> <external parts/wardrobe_top_jan.FCStd>#Body003
  Placement = pos=(-4.699e-13,1.441e-13,1396) rot=(0,0,1;0rad)
FEATURE [App::Link] wardrobe_backplate_jan_corpus00  label="wardrobe_backplate_corpus01_jan"
  LinkPlacement = pos=(-3e-15,300,707.5) rot=(0,0,1;3.14159rad)
  LinkedObject = -> <external parts/wardrobe_backplate_corpus01_jan.FCStd>#Body004
  Placement = pos=(-3e-15,300,707.5) rot=(0,0,1;3.14159rad)
FEATURE [App::FeaturePython] Joint002  label="StarrerVerbund002"  # Assembly joint (typed FeaturePython)
  Activated = true
  AngleMax = 0
  AngleMin = 0
  Detach1 = false
  Detach2 = false
  Distance = 0
  Distance2 = 0
  EnableAngleMax = false
  EnableAngleMin = false
  EnableLengthMax = false
  EnableLengthMin = false
  JointType = 0 (Fixed)
  LengthMax = 0
  LengthMin = 0
  Offset2 = pos=(0,0,0) rot=(0,0,1;3.14159rad)
  Placement1 = pos=(-3e-15,0,-707.5) rot=(0.707107,0,0.707107;3.14159rad)
  Placement2 = pos=(0,300,0) rot=(0,1,0;4.71239rad)
  Reference1 = -> Assembly [wardrobe_backplate_jan_corpus00.Edge3,wardrobe_backplate_jan_corpus00.Edge3]
  Reference2 = -> Assembly [wardrobe_base_jan.Edge9,wardrobe_base_jan.Edge9]
FEATURE [App::FeaturePython] Joint  label="StarrerVerbund"  # Assembly joint (typed FeaturePython)
  Activated = true
  AngleMax = 0
  AngleMin = 0
  Detach1 = false
  Detach2 = false
  Distance = 0
  Distance2 = 0
  EnableAngleMax = false
  EnableAngleMin = false
  EnableLengthMax = false
  EnableLengthMin = false
  JointType = 0 (Fixed)
  LengthMax = 0
  LengthMin = 0
  Placement1 = pos=(19,-1.01e-13,-688.5) rot=(0.57735,0.57735,0.57735;4.18879rad)
  Placement2 = pos=(270,0,19) rot=(0.57735,0.57735,0.57735;4.18879rad)
  Reference1 = -> Assembly [wardrobe_right_jan_corpus00.Edge4,wardrobe_right_jan_corpus00.Edge4]
  Reference2 = -> Assembly [wardrobe_base_jan.Edge7,wardrobe_base_jan.Edge7]
FEATURE [App::FeaturePython] Joint003  label="StarrerVerbund003"  # Assembly joint (typed FeaturePython)
  Activated = true
  AngleMax = 0
  AngleMin = 0
  Detach1 = false
  Detach2 = false
  Distance = 0
  Distance2 = 0
  EnableAngleMax = false
  EnableAngleMin = false
  EnableLengthMax = false
  EnableLengthMin = false
  JointType = 0 (Fixed)
  LengthMax = 0
  LengthMin = 0
  Offset2 = pos=(0,0,0) rot=(0,0,1;3.14159rad)
  Placement1 = pos=(2.274e-13,-9.63e-14,-688.5) rot=(0.57735,0.57735,0.57735;4.18879rad)
  Placement2 = pos=(-270,0,19) rot=(-0.57735,0.57735,-0.57735;4.18879rad)
  Reference1 = -> Assembly [wardrobe_left_jan_corpus00.Edge3,wardrobe_left_jan_corpus00.Edge3]
  Reference2 = -> Assembly [wardrobe_base_jan.Edge12,wardrobe_base_jan.Edge12]
FEATURE [App::FeaturePython] Joint004  label="StarrerVerbund004"  # Assembly joint (typed FeaturePython)
  Activated = true
  AngleMax = 0
  AngleMin = 0
  Detach1 = false
  Detach2 = false
  Distance = 0
  Distance2 = 0
  EnableAngleMax = false
  EnableAngleMin = false
  EnableLengthMax = false
  EnableLengthMin = false
  JointType = 0 (Fixed)
  LengthMax = 0
  LengthMin = 0
  Offset2 = pos=(0,0,0) rot=(0,0,1;3.14159rad)
  Placement1 = pos=(270,2.33e-14,0) rot=(0.57735,0.57735,0.57735;4.18879rad)
  Placement2 = pos=(19,1.264e-13,688.5) rot=(-0.57735,0.57735,-0.57735;4.18879rad)
  Reference1 = -> Assembly [wardrobe_top_jan.Edge6,wardrobe_top_jan.Edge6]
  Reference2 = -> Assembly [wardrobe_right_jan_corpus00.Edge10,wardrobe_right_jan_corpus00.Edge10]
FEATURE [App::Link] hettich_level_adjustment  label="hettich-level-adjustment"
  LinkPlacement = pos=(-218.25,-240,-1.33e-14) rot=(0.707107,0.707107,0;3.14159rad)
  LinkedObject = -> <external ../purchased parts/hettich-level-adjustment.FCStd>#Body
  Placement = pos=(-218.25,-240,-1.33e-14) rot=(0.707107,0.707107,0;3.14159rad)
FEATURE [App::Link] hettich_level_adjustment001  label="hettich-level-adjustment001"
  LinkPlacement = pos=(218.25,-240,1.33e-14) rot=(0.707107,-0.707107,0;3.14159rad)
  LinkedObject = -> <external ../purchased parts/hettich-level-adjustment.FCStd>#Body
  Placement = pos=(218.25,-240,1.33e-14) rot=(0.707107,-0.707107,0;3.14159rad)
FEATURE [App::Link] hettich_level_adjustment002  label="hettich-level-adjustment002"
  LinkPlacement = pos=(218.25,240,-1.33e-14) rot=(0.707107,-0.707107,0;3.14159rad)
  LinkedObject = -> <external ../purchased parts/hettich-level-adjustment.FCStd>#Body
  Placement = pos=(218.25,240,-1.33e-14) rot=(0.707107,-0.707107,0;3.14159rad)
FEATURE [App::Link] hettich_level_adjustment003  label="hettich-level-adjustment003"
  LinkPlacement = pos=(-218.25,240,1.33e-14) rot=(0.707107,0.707107,0;3.14159rad)
  LinkedObject = -> <external ../purchased parts/hettich-level-adjustment.FCStd>#Body
  Placement = pos=(-218.25,240,1.33e-14) rot=(0.707107,0.707107,0;3.14159rad)
FEATURE [App::FeaturePython] Joint005  label="StarrerVerbund005"  # Assembly joint (typed FeaturePython)
  Activated = true
  AngleMax = 0
  AngleMin = 0
  Detach1 = false
  Detach2 = false
  Distance = 0
  Distance2 = 0
  EnableAngleMax = false
  EnableAngleMin = false
  EnableLengthMax = false
  EnableLengthMin = false
  JointType = 0 (Fixed)
  LengthMax = 0
  LengthMin = 0
  Offset1 = pos=(0,20,-60) rot=(0,0,1;0rad)
  Placement1 = pos=(-60,-51.75,0) rot=(0.707107,0,0.707107;3.14159rad)
  Placement2 = pos=(-270,-300,0) rot=(-0.57735,-0.57735,0.57735;4.18879rad)
  Reference1 = -> Assembly [hettich_level_adjustment.Edge10,hettich_level_adjustment.Edge10]
  Reference2 = -> Assembly [wardrobe_base_jan.Edge11,wardrobe_base_jan.Vertex1]
FEATURE [App::FeaturePython] Joint006  label="StarrerVerbund006"  # Assembly joint (typed FeaturePython)
  Activated = true
  AngleMax = 0
  AngleMin = 0
  Detach1 = false
  Detach2 = false
  Distance = 0
  Distance2 = 0
  EnableAngleMax = false
  EnableAngleMin = false
  EnableLengthMax = false
  EnableLengthMin = false
  JointType = 0 (Fixed)
  LengthMax = 0
  LengthMin = 0
  Offset1 = pos=(0,20,60) rot=(0,0,1;0rad)
  Offset2 = pos=(0,0,0) rot=(0,0,1;3.14159rad)
  Placement1 = pos=(60,-51.75,0) rot=(0.707107,0,0.707107;3.14159rad)
  Placement2 = pos=(270,-300,0) rot=(0.57735,-0.57735,-0.57735;4.18879rad)
  Reference1 = -> Assembly [hettich_level_adjustment001.Edge10,hettich_level_adjustment001.Edge10]
  Reference2 = -> Assembly [wardrobe_base_jan.Edge6,wardrobe_base_jan.Vertex3]
FEATURE [App::FeaturePython] Joint007  label="StarrerVerbund007"  # Assembly joint (typed FeaturePython)
  Activated = true
  AngleMax = 0
  AngleMin = 0
  Detach1 = false
  Detach2 = false
  Distance = 0
  Distance2 = 0
  EnableAngleMax = false
  EnableAngleMin = false
  EnableLengthMax = false
  EnableLengthMin = false
  JointType = 0 (Fixed)
  LengthMax = 0
  LengthMin = 0
  Offset1 = pos=(0,20,-60) rot=(0,0,1;0rad)
  Offset2 = pos=(0,0,0) rot=(0,0,1;3.14159rad)
  Placement1 = pos=(-60,-51.75,0) rot=(0.707107,0,0.707107;3.14159rad)
  Placement2 = pos=(270,300,0) rot=(0.57735,-0.57735,-0.57735;4.18879rad)
  Reference1 = -> Assembly [hettich_level_adjustment002.Edge10,hettich_level_adjustment002.Edge10]
  Reference2 = -> Assembly [wardrobe_base_jan.Edge6,wardrobe_base_jan.Vertex5]
FEATURE [App::FeaturePython] Joint008  label="StarrerVerbund008"  # Assembly joint (typed FeaturePython)
  Activated = true
  AngleMax = 0
  AngleMin = 0
  Detach1 = false
  Detach2 = false
  Distance = 0
  Distance2 = 0
  EnableAngleMax = false
  EnableAngleMin = false
  EnableLengthMax = false
  EnableLengthMin = false
  JointType = 0 (Fixed)
  LengthMax = 0
  LengthMin = 0
  Offset1 = pos=(0,20,60) rot=(0,0,1;0rad)
  Placement1 = pos=(60,-51.75,0) rot=(0.707107,0,0.707107;3.14159rad)
  Placement2 = pos=(-270,300,0) rot=(-0.57735,-0.57735,0.57735;4.18879rad)
  Reference1 = -> Assembly [hettich_level_adjustment003.Edge10,hettich_level_adjustment003.Edge10]
  Reference2 = -> Assembly [wardrobe_base_jan.Edge11,wardrobe_base_jan.Vertex7]
FEATURE [App::Link] wardrobe_door_corpus01_jan
  LinkPlacement = pos=(267.5,-300,-2.1e-15) rot=(1,0,0;1.5708rad)
  LinkedObject = -> <external parts/wardrobe_door_corpus01_jan.FCStd>#Body
  Placement = pos=(267.5,-300,-2.1e-15) rot=(1,0,0;1.5708rad)
FEATURE [App::FeaturePython] Joint009  label="Parallel"  # Assembly joint (typed FeaturePython)
  Activated = true
  AngleMax = 0
  AngleMin = 0
  Detach1 = false
  Detach2 = false
  Distance = 0
  Distance2 = 0
  EnableAngleMax = false
  EnableAngleMin = false
  EnableLengthMax = false
  EnableLengthMin = false
  JointType = 6 (Parallel)
  LengthMax = 0
  LengthMin = 0
  Placement1 = pos=(270,-300,19) rot=(-1,0,0;1.5708rad)
  Placement2 = pos=(-251.391,875.698,0) rot=(0,0,1;0rad)
  Reference1 = -> Assembly [wardrobe_top_jan.Face1,wardrobe_top_jan.Vertex4]
  Reference2 = -> Assembly [wardrobe_door_corpus01_jan.Face5,wardrobe_door_corpus01_jan.Face5]
FEATURE [App::FeaturePython] Joint010  label="Parallel001"  # Assembly joint (typed FeaturePython)
  Activated = true
  AngleMax = 0
  AngleMin = 0
  Detach1 = false
  Detach2 = false
  Distance = 0
  Distance2 = 0
  EnableAngleMax = false
  EnableAngleMin = false
  EnableLengthMax = false
  EnableLengthMin = false
  JointType = 6 (Parallel)
  LengthMax = 0
  LengthMin = 0
  Placement1 = pos=(0,1022.77,9.5) rot=(-0.57735,-0.57735,0.57735;2.0944rad)
  Placement2 = pos=(19,1.137e-13,0) rot=(0.707107,0,0.707107;3.14159rad)
  Reference1 = -> Assembly [wardrobe_door_corpus01_jan.Face1,wardrobe_door_corpus01_jan.Face1]
  Reference2 = -> Assembly [wardrobe_right_jan_corpus00.Face6,wardrobe_right_jan_corpus00.Face6]
FEATURE [App::FeaturePython] Joint011  label="Parallel002"  # Assembly joint (typed FeaturePython)
  Activated = true
  AngleMax = 0
  AngleMin = 0
  Detach1 = false
  Detach2 = false
  Distance = 0
  Distance2 = 0
  EnableAngleMax = false
  EnableAngleMin = false
  EnableLengthMax = false
  EnableLengthMin = false
  JointType = 6 (Parallel)
  LengthMax = 0
  LengthMin = 0
  Placement1 = pos=(-267.5,0,9.5) rot=(0,0.707107,-0.707107;3.14159rad)
  Placement2 = pos=(270,-300,0) rot=(0,0,1;0rad)
  Reference1 = -> Assembly [wardrobe_door_corpus01_jan.Face4,wardrobe_door_corpus01_jan.Face4]
  Reference2 = -> Assembly [wardrobe_base_jan.Face5,wardrobe_base_jan.Vertex3]
FEATURE [App::FeaturePython] Joint012  label="Abstand"  # Assembly joint (typed FeaturePython)
  Activated = true
  AngleMax = 0
  AngleMin = 0
  Detach1 = false
  Detach2 = false
  Distance = 0
  Distance2 = 0
  EnableAngleMax = false
  EnableAngleMin = false
  EnableLengthMax = false
  EnableLengthMin = false
  JointType = 5 (Distance)
  LengthMax = 0
  LengthMin = 0
  Placement1 = pos=(-251.391,875.698,0) rot=(0,0,1;0rad)
  Placement2 = pos=(-1.33e-14,-300,9.5) rot=(-1,0,0;1.5708rad)
  Reference1 = -> Assembly [wardrobe_door_corpus01_jan.Face5,wardrobe_door_corpus01_jan.Face5]
  Reference2 = -> Assembly [wardrobe_top_jan.Face1,wardrobe_top_jan.Vertex3]
FEATURE [App::FeaturePython] Joint013  label="Abstand001"  # Assembly joint (typed FeaturePython)
  Activated = true
  AngleMax = 0
  AngleMin = 0
  Detach1 = false
  Detach2 = false
  Distance = 2.5
  Distance2 = 0
  EnableAngleMax = false
  EnableAngleMin = false
  EnableLengthMax = false
  EnableLengthMin = false
  JointType = 5 (Distance)
  LengthMax = 0
  LengthMin = 0
  Placement1 = pos=(-535,709.772,9.5) rot=(-0.57735,-0.57735,0.57735;2.0944rad)
  Placement2 = pos=(0,9.72e-14,0) rot=(0.707107,0,0.707107;3.14159rad)
  Reference1 = -> Assembly [wardrobe_door_corpus01_jan.Face3,wardrobe_door_corpus01_jan.Vertex5]
  Reference2 = -> Assembly [wardrobe_left_jan_corpus00.Face5,wardrobe_left_jan_corpus00.Vertex7]
FEATURE [App::FeaturePython] Joint014  label="Abstand002"  # Assembly joint (typed FeaturePython)
  Activated = true
  AngleMax = 0
  AngleMin = 0
  Detach1 = false
  Detach2 = false
  Distance = 0
  Distance2 = 0
  EnableAngleMax = false
  EnableAngleMin = false
  EnableLengthMax = false
  EnableLengthMin = false
  JointType = 5 (Distance)
  LengthMax = 0
  LengthMin = 0
  Placement1 = pos=(-267.5,0,9.5) rot=(0,0.707107,-0.707107;3.14159rad)
  Placement2 = pos=(-1.3e-15,0,0) rot=(0,0,1;0rad)
  Reference1 = -> Assembly [wardrobe_door_corpus01_jan.Face4,wardrobe_door_corpus01_jan.Vertex7]
  Reference2 = -> Assembly [wardrobe_base_jan.Face5,wardrobe_base_jan.Vertex1]
FEATURE [Assembly::JointGroup] Joints
  Group = -> [GroundedJoint,Joint002,Joint,Joint003,Joint004,Joint005,Joint006,Joint007,Joint008,Joint009,Joint010,Joint011,Joint012,Joint013,Joint014]
FEATURE [Assembly::AssemblyObject] Assembly  label="wardrobe_corpus01_jan"
  Group = -> [Joints,wardrobe_base_jan,GroundedJoint,wardrobe_right_jan_corpus00,wardrobe_left_jan_corpus00,wardrobe_top_jan,wardrobe_backplate_jan_corpus00,Joint002,Joint,Joint003,Joint004,hettich_level_adjustment,hettich_level_adjustment001,hettich_level_adjustment002,hettich_level_adjustment003,Joint005,Joint006,Joint007,Joint008,wardrobe_door_corpus01_jan,Joint009,Joint010,Joint011,Joint012,Joint013,+1 more]
  Origin = -> Origin
  Type = Assembly
---- part subassemblies/wardrobe_corpus02_jan.FCStd = doc fcstd_c93ad19bde4e ----
FCSTD DOCUMENT  (FreeCAD 1.0RUnknown)
Label: wardrobe_corpus02_jan
License: All rights reserved
LicenseURL: https://en.wikipedia.org/wiki/All_rights_reserved
objects: App::FeaturePython×15, App::Link×10, Assembly::JointGroup×1, Assembly::AssemblyObject×1
EXTERNAL_REF file=parts/wardrobe_base_jan.FCStd obj=Body
EXTERNAL_REF file=parts/wardrobe_right_corpus02_jan.FCStd obj=Body002
EXTERNAL_REF file=parts/wardrobe_left_corpus02_jan.FCStd obj=Body001
EXTERNAL_REF file=parts/wardrobe_top_jan.FCStd obj=Body003
EXTERNAL_REF file=parts/wardrobe_backplate_corpus02_jan.FCStd obj=Body004
EXTERNAL_REF file=../purchased parts/hettich-level-adjustment.FCStd obj=Body
EXTERNAL_REF file=parts/wardrobe_door_corpus02_jan.FCStd obj=Body

FEATURE [App::Link] wardrobe_base_jan
  LinkedObject = -> <external parts/wardrobe_base_jan.FCStd>#Body
FEATURE [App::FeaturePython] GroundedJoint  # Assembly grounded joint (typed FeaturePython)
  ObjectToGround = -> wardrobe_base_jan
FEATURE [App::Link] wardrobe_right_jan_corpus00  label="wardrobe_right_corpus02_jan"
  LinkPlacement = pos=(251,-5.11e-14,390) rot=(0,0,1;0rad)
  LinkedObject = -> <external parts/wardrobe_right_corpus02_jan.FCStd>#Body002
  Placement = pos=(251,-5.11e-14,390) rot=(0,0,1;0rad)
FEATURE [App::Link] wardrobe_left_jan_corpus00  label="wardrobe_left_corpus02_jan"
  LinkPlacement = pos=(-270,9.63e-14,390) rot=(0,0,1;0rad)
  LinkedObject = -> <external parts/wardrobe_left_corpus02_jan.FCStd>#Body001
  Placement = pos=(-270,9.63e-14,390) rot=(0,0,1;0rad)
FEATURE [App::Link] wardrobe_top_jan
  LinkPlacement = pos=(-2.095e-13,-1.636e-13,761) rot=(0,0,1;0rad)
  LinkedObject = -> <external parts/wardrobe_top_jan.FCStd>#Body003
  Placement = pos=(-2.095e-13,-1.636e-13,761) rot=(0,0,1;0rad)
FEATURE [App::Link] wardrobe_backplate_jan_corpus00  label="wardrobe_backplate_corpus02_jan"
  LinkPlacement = pos=(-3e-15,300,390) rot=(0,0,1;3.14159rad)
  LinkedObject = -> <external parts/wardrobe_backplate_corpus02_jan.FCStd>#Body004
  Placement = pos=(-3e-15,300,390) rot=(0,0,1;3.14159rad)
FEATURE [App::FeaturePython] Joint002  label="StarrerVerbund002"  # Assembly joint (typed FeaturePython)
  Activated = true
  AngleMax = 0
  AngleMin = 0
  Detach1 = false
  Detach2 = false
  Distance = 0
  Distance2 = 0
  EnableAngleMax = false
  EnableAngleMin = false
  EnableLengthMax = false
  EnableLengthMin = false
  JointType = 0 (Fixed)
  LengthMax = 0
  LengthMin = 0
  Offset2 = pos=(0,0,0) rot=(0,0,1;3.14159rad)
  Placement1 = pos=(-3e-15,0,-390) rot=(0.707107,0,0.707107;3.14159rad)
  Placement2 = pos=(0,300,0) rot=(0,1,0;4.71239rad)
  Reference1 = -> Assembly [wardrobe_backplate_jan_corpus00.Edge3,wardrobe_backplate_jan_corpus00.Edge3]
  Reference2 = -> Assembly [wardrobe_base_jan.Edge9,wardrobe_base_jan.Edge9]
FEATURE [App::FeaturePython] Joint  label="StarrerVerbund"  # Assembly joint (typed FeaturePython)
  Activated = true
  AngleMax = 0
  AngleMin = 0
  Detach1 = false
  Detach2 = false
  Distance = 0
  Distance2 = 0
  EnableAngleMax = false
  EnableAngleMin = false
  EnableLengthMax = false
  EnableLengthMin = false
  JointType = 0 (Fixed)
  LengthMax = 0
  LengthMin = 0
  Placement1 = pos=(19,-1.137e-13,-371) rot=(0.57735,0.57735,0.57735;4.18879rad)
  Placement2 = pos=(270,0,19) rot=(0.57735,0.57735,0.57735;4.18879rad)
  Reference1 = -> Assembly [wardrobe_right_jan_corpus00.Edge4,wardrobe_right_jan_corpus00.Edge4]
  Reference2 = -> Assembly [wardrobe_base_jan.Edge7,wardrobe_base_jan.Edge7]
FEATURE [App::FeaturePython] Joint003  label="StarrerVerbund003"  # Assembly joint (typed FeaturePython)
  Activated = true
  AngleMax = 0
  AngleMin = 0
  Detach1 = false
  Detach2 = false
  Distance = 0
  Distance2 = 0
  EnableAngleMax = false
  EnableAngleMin = false
  EnableLengthMax = false
  EnableLengthMin = false
  JointType = 0 (Fixed)
  LengthMax = 0
  LengthMin = 0
  Offset2 = pos=(0,0,0) rot=(0,0,1;3.14159rad)
  Placement1 = pos=(1.137e-13,-9.63e-14,-371) rot=(0.57735,0.57735,0.57735;4.18879rad)
  Placement2 = pos=(-270,0,19) rot=(-0.57735,0.57735,-0.57735;4.18879rad)
  Reference1 = -> Assembly [wardrobe_left_jan_corpus00.Edge3,wardrobe_left_jan_corpus00.Edge3]
  Reference2 = -> Assembly [wardrobe_base_jan.Edge12,wardrobe_base_jan.Edge12]
FEATURE [App::FeaturePython] Joint004  label="StarrerVerbund004"  # Assembly joint (typed FeaturePython)
  Activated = true
  AngleMax = 0
  AngleMin = 0
  Detach1 = false
  Detach2 = false
  Distance = 0
  Distance2 = 0
  EnableAngleMax = false
  EnableAngleMin = false
  EnableLengthMax = false
  EnableLengthMin = false
  JointType = 0 (Fixed)
  LengthMax = 0
  LengthMin = 0
  Offset2 = pos=(0,0,0) rot=(0,0,1;3.14159rad)
  Placement1 = pos=(270,1.5e-15,0) rot=(0.57735,0.57735,0.57735;4.18879rad)
  Placement2 = pos=(19,1.137e-13,371) rot=(-0.57735,0.57735,-0.57735;4.18879rad)
  Reference1 = -> Assembly [wardrobe_top_jan.Edge6,wardrobe_top_jan.Edge6]
  Reference2 = -> Assembly [wardrobe_right_jan_corpus00.Edge10,wardrobe_right_jan_corpus00.Edge10]
FEATURE [App::Link] hettich_level_adjustment  label="hettich-level-adjustment"
  LinkPlacement = pos=(-218.25,-240,-1.33e-14) rot=(0.707107,0.707107,0;3.14159rad)
  LinkedObject = -> <external ../purchased parts/hettich-level-adjustment.FCStd>#Body
  Placement = pos=(-218.25,-240,-1.33e-14) rot=(0.707107,0.707107,0;3.14159rad)
FEATURE [App::Link] hettich_level_adjustment001  label="hettich-level-adjustment001"
  LinkPlacement = pos=(218.25,-240,-3.9e-15) rot=(-0.707107,0.707107,0;3.14159rad)
  LinkedObject = -> <external ../purchased parts/hettich-level-adjustment.FCStd>#Body
  Placement = pos=(218.25,-240,-3.9e-15) rot=(-0.707107,0.707107,0;3.14159rad)
FEATURE [App::Link] hettich_level_adjustment002  label="hettich-level-adjustment002"
  LinkPlacement = pos=(218.25,240,-1.97e-14) rot=(0.707107,-0.707107,0;3.14159rad)
  LinkedObject = -> <external ../purchased parts/hettich-level-adjustment.FCStd>#Body
  Placement = pos=(218.25,240,-1.97e-14) rot=(0.707107,-0.707107,0;3.14159rad)
FEATURE [App::Link] hettich_level_adjustment003  label="hettich-level-adjustment003"
  LinkPlacement = pos=(-218.25,240,1.33e-14) rot=(0.707107,0.707107,0;3.14159rad)
  LinkedObject = -> <external ../purchased parts/hettich-level-adjustment.FCStd>#Body
  Placement = pos=(-218.25,240,1.33e-14) rot=(0.707107,0.707107,0;3.14159rad)
FEATURE [App::FeaturePython] Joint005  label="StarrerVerbund005"  # Assembly joint (typed FeaturePython)
  Activated = true
  AngleMax = 0
  AngleMin = 0
  Detach1 = false
  Detach2 = false
  Distance = 0
  Distance2 = 0
  EnableAngleMax = false
  EnableAngleMin = false
  EnableLengthMax = false
  EnableLengthMin = false
  JointType = 0 (Fixed)
  LengthMax = 0
  LengthMin = 0
  Offset1 = pos=(0,20,-60) rot=(0,0,1;0rad)
  Placement1 = pos=(-60,-51.75,0) rot=(0.707107,0,0.707107;3.14159rad)
  Placement2 = pos=(-270,-300,0) rot=(-0.57735,-0.57735,0.57735;4.18879rad)
  Reference1 = -> Assembly [hettich_level_adjustment.Edge10,hettich_level_adjustment.Edge10]
  Reference2 = -> Assembly [wardrobe_base_jan.Edge11,wardrobe_base_jan.Vertex1]
FEATURE [App::FeaturePython] Joint006  label="StarrerVerbund006"  # Assembly joint (typed FeaturePython)
  Activated = true
  AngleMax = 0
  AngleMin = 0
  Detach1 = false
  Detach2 = false
  Distance = 0
  Distance2 = 0
  EnableAngleMax = false
  EnableAngleMin = false
  EnableLengthMax = false
  EnableLengthMin = false
  JointType = 0 (Fixed)
  LengthMax = 0
  LengthMin = 0
  Offset1 = pos=(0,-20,60) rot=(0,0,1;0rad)
  Offset2 = pos=(0,0,0) rot=(0,0,1;3.14159rad)
  Placement1 = pos=(250,-240,0) rot=(0.57735,0.57735,0.57735;4.18879rad)
  Placement2 = pos=(0,-31.75,0) rot=(0,-1,0;4.71239rad)
  Reference1 = -> Assembly [wardrobe_base_jan.Edge6,wardrobe_base_jan.Vertex3]
  Reference2 = -> Assembly [hettich_level_adjustment001.Edge10,hettich_level_adjustment001.Edge10]
FEATURE [App::FeaturePython] Joint007  label="StarrerVerbund007"  # Assembly joint (typed FeaturePython)
  Activated = true
  AngleMax = 0
  AngleMin = 0
  Detach1 = false
  Detach2 = false
  Distance = 0
  Distance2 = 0
  EnableAngleMax = false
  EnableAngleMin = false
  EnableLengthMax = false
  EnableLengthMin = false
  JointType = 0 (Fixed)
  LengthMax = 0
  LengthMin = 0
  Offset1 = pos=(0,20,-60) rot=(0,0,1;3.14159rad)
  Placement1 = pos=(-60,-51.75,0) rot=(0,-1,0;4.71239rad)
  Placement2 = pos=(270,300,0) rot=(0.57735,0.57735,0.57735;4.18879rad)
  Reference1 = -> Assembly [hettich_level_adjustment002.Edge10,hettich_level_adjustment002.Edge10]
  Reference2 = -> Assembly [wardrobe_base_jan.Edge6,wardrobe_base_jan.Vertex5]
FEATURE [App::FeaturePython] Joint008  label="StarrerVerbund008"  # Assembly joint (typed FeaturePython)
  Activated = true
  AngleMax = 0
  AngleMin = 0
  Detach1 = false
  Detach2 = false
  Distance = 0
  Distance2 = 0
  EnableAngleMax = false
  EnableAngleMin = false
  EnableLengthMax = false
  EnableLengthMin = false
  JointType = 0 (Fixed)
  LengthMax = 0
  LengthMin = 0
  Offset1 = pos=(0,20,60) rot=(0,0,1;0rad)
  Placement1 = pos=(60,-51.75,0) rot=(0.707107,0,0.707107;3.14159rad)
  Placement2 = pos=(-270,300,0) rot=(-0.57735,-0.57735,0.57735;4.18879rad)
  Reference1 = -> Assembly [hettich_level_adjustment003.Edge10,hettich_level_adjustment003.Edge10]
  Reference2 = -> Assembly [wardrobe_base_jan.Edge11,wardrobe_base_jan.Vertex7]
FEATURE [App::Link] wardrobe_door_corpus02_jan
  LinkPlacement = pos=(267.5,-300,2.1e-15) rot=(1,0,0;1.5708rad)
  LinkedObject = -> <external parts/wardrobe_door_corpus02_jan.FCStd>#Body
  Placement = pos=(267.5,-300,2.1e-15) rot=(1,0,0;1.5708rad)
FEATURE [App::FeaturePython] Joint009  label="Parallel"  # Assembly joint (typed FeaturePython)
  Activated = true
  AngleMax = 0
  AngleMin = 0
  Detach1 = false
  Detach2 = false
  Distance = 0
  Distance2 = 0
  EnableAngleMax = false
  EnableAngleMin = false
  EnableLengthMax = false
  EnableLengthMin = false
  JointType = 6 (Parallel)
  LengthMax = 0
  LengthMin = 0
  Placement1 = pos=(-242.144,565.18,0) rot=(0,0,1;0rad)
  Placement2 = pos=(5.4e-15,-300,9.5) rot=(-1,0,0;1.5708rad)
  Reference1 = -> Assembly [wardrobe_door_corpus02_jan.Face5,wardrobe_door_corpus02_jan.Face5]
  Reference2 = -> Assembly [wardrobe_top_jan.Face1,wardrobe_top_jan.Face1]
FEATURE [App::FeaturePython] Joint010  label="Parallel001"  # Assembly joint (typed FeaturePython)
  Activated = true
  AngleMax = 0
  AngleMin = 0
  Detach1 = false
  Detach2 = false
  Distance = 0
  Distance2 = 0
  EnableAngleMax = false
  EnableAngleMin = false
  EnableLengthMax = false
  EnableLengthMin = false
  JointType = 6 (Parallel)
  LengthMax = 0
  LengthMin = 0
  Placement1 = pos=(0,706.847,9.5) rot=(-0.57735,-0.57735,0.57735;2.0944rad)
  Placement2 = pos=(19,1.018e-13,0) rot=(0.707107,0,0.707107;3.14159rad)
  Reference1 = -> Assembly [wardrobe_door_corpus02_jan.Face1,wardrobe_door_corpus02_jan.Face1]
  Reference2 = -> Assembly [wardrobe_right_jan_corpus00.Face6,wardrobe_right_jan_corpus00.Face6]
FEATURE [App::FeaturePython] Joint011  label="Parallel002"  # Assembly joint (typed FeaturePython)
  Activated = true
  AngleMax = 0
  AngleMin = 0
  Detach1 = false
  Detach2 = false
  Distance = 0
  Distance2 = 0
  EnableAngleMax = false
  EnableAngleMin = false
  EnableLengthMax = false
  EnableLengthMin = false
  JointType = 6 (Parallel)
  LengthMax = 0
  LengthMin = 0
  Placement1 = pos=(-267.5,0,9.5) rot=(0,0.707107,-0.707107;3.14159rad)
  Placement2 = pos=(-1.3e-15,0,0) rot=(0,0,1;0rad)
  Reference1 = -> Assembly [wardrobe_door_corpus02_jan.Face4,wardrobe_door_corpus02_jan.Face4]
  Reference2 = -> Assembly [wardrobe_base_jan.Face5,wardrobe_base_jan.Face5]
FEATURE [App::FeaturePython] Joint012  label="Abstand"  # Assembly joint (typed FeaturePython)
  Activated = true
  AngleMax = 0
  AngleMin = 0
  Detach1 = false
  Detach2 = false
  Distance = 0
  Distance2 = 0
  EnableAngleMax = false
  EnableAngleMin = false
  EnableLengthMax = false
  EnableLengthMin = false
  JointType = 5 (Distance)
  LengthMax = 0
  LengthMin = 0
  Placement1 = pos=(-267.5,0,9.5) rot=(0,0.707107,-0.707107;3.14159rad)
  Placement2 = pos=(-1.3e-15,0,0) rot=(0,0,1;0rad)
  Reference1 = -> Assembly [wardrobe_door_corpus02_jan.Face4,wardrobe_door_corpus02_jan.Face4]
  Reference2 = -> Assembly [wardrobe_base_jan.Face5,wardrobe_base_jan.Face5]
FEATURE [App::FeaturePython] Joint013  label="Abstand001"  # Assembly joint (typed FeaturePython)
  Activated = true
  AngleMax = 0
  AngleMin = 0
  Detach1 = false
  Detach2 = false
  Distance = -2.5
  Distance2 = 0
  EnableAngleMax = false
  EnableAngleMin = false
  EnableLengthMax = false
  EnableLengthMin = false
  JointType = 5 (Distance)
  LengthMax = 0
  LengthMin = 0
  Placement1 = pos=(19,1.018e-13,0) rot=(0.707107,0,0.707107;3.14159rad)
  Placement2 = pos=(0,706.847,9.5) rot=(-0.57735,-0.57735,0.57735;2.0944rad)
  Reference1 = -> Assembly [wardrobe_right_jan_corpus00.Face6,wardrobe_right_jan_corpus00.Vertex2]
  Reference2 = -> Assembly [wardrobe_door_corpus02_jan.Face1,wardrobe_door_corpus02_jan.Face1]
FEATURE [App::FeaturePython] Joint014  label="Abstand002"  # Assembly joint (typed FeaturePython)
  Activated = true
  AngleMax = 0
  AngleMin = 0
  Detach1 = false
  Detach2 = false
  Distance = 0
  Distance2 = 0
  EnableAngleMax = false
  EnableAngleMin = false
  EnableLengthMax = false
  EnableLengthMin = false
  JointType = 5 (Distance)
  LengthMax = 0
  LengthMin = 0
  Placement1 = pos=(-242.144,565.18,0) rot=(0,0,1;0rad)
  Placement2 = pos=(5.4e-15,-300,9.5) rot=(-1,0,0;1.5708rad)
  Reference1 = -> Assembly [wardrobe_door_corpus02_jan.Face5,wardrobe_door_corpus02_jan.Face5]
  Reference2 = -> Assembly [wardrobe_top_jan.Face1,wardrobe_top_jan.Vertex1]
FEATURE [Assembly::JointGroup] Joints
  Group = -> [GroundedJoint,Joint002,Joint,Joint003,Joint004,Joint005,Joint006,Joint007,Joint008,Joint009,Joint010,Joint011,Joint012,Joint013,Joint014]
FEATURE [Assembly::AssemblyObject] Assembly  label="wardrobe_corpus02_jan"
  Group = -> [Joints,wardrobe_base_jan,GroundedJoint,wardrobe_right_jan_corpus00,wardrobe_left_jan_corpus00,wardrobe_top_jan,wardrobe_backplate_jan_corpus00,Joint002,Joint,Joint003,Joint004,hettich_level_adjustment,hettich_level_adjustment001,hettich_level_adjustment002,hettich_level_adjustment003,Joint005,Joint006,Joint007,Joint008,wardrobe_door_corpus02_jan,Joint009,Joint010,Joint011,Joint012,Joint013,+1 more]
  Origin = -> Origin
  Type = Assembly
---- part subassemblies/wardrobe_drawer_jan.FCStd = doc fcstd_7002e96fd710 ----
FCSTD DOCUMENT  (FreeCAD 1.0RUnknown)
Label: wardrobe_drawer_jan
License: All rights reserved
objects: App::FeaturePython×11, App::Link×7, Assembly::JointGroup×1, Assembly::AssemblyObject×1
EXTERNAL_REF file=../purchased parts/hettich_rail_550mm.FCStd obj=Body
EXTERNAL_REF file=parts/drawer_sides.FCStd obj=Body
EXTERNAL_REF file=parts/drawer_back.FCStd obj=Body
EXTERNAL_REF file=parts/drawer_bottom.FCStd obj=Body
EXTERNAL_REF file=parts/drawer_front.FCStd obj=Body

FEATURE [App::Link] hettich_rail_550
  LinkPlacement = pos=(0,-8.67788e-07,0) rot=(0.57735,0.57735,0.57735;2.0944rad)
  LinkedObject = -> <external ../purchased parts/hettich_rail_550mm.FCStd>#Body
  Placement = pos=(0,-8.67788e-07,0) rot=(0.57735,0.57735,0.57735;2.0944rad)
FEATURE [App::Link] hettich_rail_551  label="hettich_rail_550_1"
  LinkPlacement = pos=(502,3.32992e-05,-3.4167e-05) rot=(0.57735,-0.57735,-0.57735;2.0944rad)
  LinkedObject = -> <external ../purchased parts/hettich_rail_550mm.FCStd>#Body
  Placement = pos=(502,3.32992e-05,-3.4167e-05) rot=(0.57735,-0.57735,-0.57735;2.0944rad)
FEATURE [App::Link] drawer_sides
  LinkPlacement = pos=(22,256,72.5) rot=(-0.340731,0.659269,0.659269;0rad)
  LinkedObject = -> <external parts/drawer_sides.FCStd>#Body
  Placement = pos=(22,256,72.5) rot=(-0.340731,0.659269,0.659269;0rad)
FEATURE [App::Link] drawer_sides001
  LinkPlacement = pos=(480,-256,72.5) rot=(0,0,1;3.14159rad)
  LinkedObject = -> <external parts/drawer_sides.FCStd>#Body
  Placement = pos=(480,-256,72.5) rot=(0,0,1;3.14159rad)
FEATURE [App::Link] drawer_back
  LinkPlacement = pos=(489.5,265.5,80.75) rot=(0,0,-1;1.5708rad)
  LinkedObject = -> <external parts/drawer_back.FCStd>#Body
  Placement = pos=(489.5,265.5,80.75) rot=(0,0,-1;1.5708rad)
FEATURE [App::Link] drawer_bottom
  LinkPlacement = pos=(251,5.75002,-2.50002) rot=(0,0,1;3.14159rad)
  LinkedObject = -> <external parts/drawer_bottom.FCStd>#Body
  Placement = pos=(251,5.75002,-2.50002) rot=(0,0,1;3.14159rad)
FEATURE [App::Link] drawer_front
  LinkPlacement = pos=(12.5,-265.5,72.5) rot=(0,0,1;1.5708rad)
  LinkedObject = -> <external parts/drawer_front.FCStd>#Body
  Placement = pos=(12.5,-265.5,72.5) rot=(0,0,1;1.5708rad)
FEATURE [App::FeaturePython] GroundedJoint  # Assembly grounded joint (typed FeaturePython)
  ObjectToGround = -> hettich_rail_550
  Placement = pos=(0,-8.67788e-07,0) rot=(0.57735,0.57735,0.57735;2.0944rad)
FEATURE [App::FeaturePython] Joint  label="Gleitverbindung"  # Assembly joint (typed FeaturePython)
  Activated = true
  AngleMax = 0
  AngleMin = 0
  Detach1 = false
  Detach2 = false
  Distance = 0
  Distance2 = 0
  EnableAngleMax = false
  EnableAngleMin = false
  EnableLengthMax = true
  EnableLengthMin = true
  JointType = 3 (Slider)
  LengthMax = 275
  LengthMin = -100
  Offset2 = pos=(0,0,0) rot=(0,0,1;1.5708rad)
  Placement1 = pos=(-9.5,-256,-85) rot=(-0.57735,-0.57735,0.57735;4.18879rad)
  Placement2 = pos=(-275,-12.5,12.5) rot=(-0.57735,0.57735,0.57735;4.18879rad)
  Reference1 = -> Assembly [drawer_sides.Edge8,drawer_sides.Edge8]
  Reference2 = -> Assembly [hettich_rail_550.Edge16,hettich_rail_550.Vertex11]
FEATURE [App::FeaturePython] Joint003  label="Parallel"  # Assembly joint (typed FeaturePython)
  Activated = true
  AngleMax = 0
  AngleMin = 0
  Detach1 = false
  Detach2 = false
  Distance = 0
  Distance2 = 0
  EnableAngleMax = false
  EnableAngleMin = false
  EnableLengthMax = false
  EnableLengthMin = false
  JointType = 6 (Parallel)
  LengthMax = 0
  LengthMin = 0
  Placement1 = pos=(275,-12.5,12.5) rot=(0,0,1;0rad)
  Placement2 = pos=(-4e-16,2.5,12.5) rot=(0,0,1;0rad)
  Reference1 = -> Assembly [hettich_rail_550.Face5,hettich_rail_550.Vertex12]
  Reference2 = -> Assembly [hettich_rail_551.Face5,hettich_rail_551.Face5]
FEATURE [App::FeaturePython] Joint004  label="Parallel001"  # Assembly joint (typed FeaturePython)
  Activated = true
  AngleMax = 0
  AngleMin = 0
  Detach1 = false
  Detach2 = false
  Distance = 0
  Distance2 = 0
  EnableAngleMax = false
  EnableAngleMin = false
  EnableLengthMax = false
  EnableLengthMin = false
  JointType = 6 (Parallel)
  LengthMax = 0
  LengthMin = 0
  Placement1 = pos=(275,-12.5,25.5) rot=(0,-0.707107,0.707107;3.14159rad)
  Placement2 = pos=(-275,-12.5,25.5) rot=(0,0.707107,-0.707107;3.14159rad)
  Reference1 = -> Assembly [hettich_rail_550.Face7,hettich_rail_550.Vertex15]
  Reference2 = -> Assembly [hettich_rail_551.Face7,hettich_rail_551.Vertex16]
FEATURE [App::FeaturePython] Joint005  label="Parallel002"  # Assembly joint (typed FeaturePython)
  Activated = true
  AngleMax = 0
  AngleMin = 0
  Detach1 = false
  Detach2 = false
  Distance = 0
  Distance2 = 0
  EnableAngleMax = false
  EnableAngleMin = false
  EnableLengthMax = false
  EnableLengthMin = false
  JointType = 6 (Parallel)
  LengthMax = 0
  LengthMin = 0
  Placement1 = pos=(275,-0.565372,6.79404) rot=(-0.707107,0,-0.707107;3.14159rad)
  Placement2 = pos=(-275,-0.565372,6.79404) rot=(-0.707107,0,0.707107;3.14159rad)
  Reference1 = -> Assembly [hettich_rail_550.Face10,hettich_rail_550.Face10]
  Reference2 = -> Assembly [hettich_rail_551.Face9,hettich_rail_551.Face9]
FEATURE [App::FeaturePython] Joint006  label="Abstand"  # Assembly joint (typed FeaturePython)
  Activated = true
  AngleMax = 0
  AngleMin = 0
  Detach1 = false
  Detach2 = false
  Distance = 0
  Distance2 = 0
  EnableAngleMax = false
  EnableAngleMin = false
  EnableLengthMax = false
  EnableLengthMin = false
  JointType = 5 (Distance)
  LengthMax = 0
  LengthMin = 0
  Placement1 = pos=(275,-0.565372,6.79404) rot=(-0.707107,0,-0.707107;3.14159rad)
  Placement2 = pos=(-275,-0.565372,6.79404) rot=(-0.707107,0,0.707107;3.14159rad)
  Reference1 = -> Assembly [hettich_rail_550.Face10,hettich_rail_550.Face10]
  Reference2 = -> Assembly [hettich_rail_551.Face9,hettich_rail_551.Face9]
FEATURE [App::FeaturePython] Joint007  label="StarrerVerbund"  # Assembly joint (typed FeaturePython)
  Activated = true
  AngleMax = 0
  AngleMin = 0
  Detach1 = false
  Detach2 = false
  Distance = 0
  Distance2 = 0
  EnableAngleMax = false
  EnableAngleMin = false
  EnableLengthMax = false
  EnableLengthMin = false
  JointType = 0 (Fixed)
  LengthMax = 0
  LengthMin = 0
  Offset2 = pos=(0,0,0) rot=(0,0,1;1.5708rad)
  Placement1 = pos=(9.5,1.8e-15,85) rot=(0,0,1;0rad)
  Placement2 = pos=(-9.5,-512,85) rot=(0.707107,0.707107,0;3.14159rad)
  Reference1 = -> Assembly [drawer_front.Edge3,drawer_front.Vertex3]
  Reference2 = -> Assembly [drawer_sides.Edge10,drawer_sides.Vertex6]
FEATURE [App::FeaturePython] Joint009  label="Gleitverbindung001"  # Assembly joint (typed FeaturePython)
  Activated = true
  AngleMax = 0
  AngleMin = 0
  Detach1 = false
  Detach2 = false
  Distance = 0
  Distance2 = 0
  EnableAngleMax = false
  EnableAngleMin = false
  EnableLengthMax = false
  EnableLengthMin = false
  JointType = 3 (Slider)
  LengthMax = 0
  LengthMin = 0
  Placement1 = pos=(275,-12.5,12.5) rot=(-0.707107,0,0.707107;3.14159rad)
  Placement2 = pos=(-9.5,-256,-85) rot=(-0.57735,-0.57735,0.57735;4.18879rad)
  Reference1 = -> Assembly [hettich_rail_551.Edge16,hettich_rail_551.Vertex12]
  Reference2 = -> Assembly [drawer_sides001.Edge8,drawer_sides001.Edge8]
FEATURE [App::FeaturePython] Joint010  label="StarrerVerbund002"  # Assembly joint (typed FeaturePython)
  Activated = true
  AngleMax = 0
  AngleMin = 0
  Detach1 = false
  Detach2 = false
  Distance = 0
  Distance2 = 0
  EnableAngleMax = false
  EnableAngleMin = false
  EnableLengthMax = false
  EnableLengthMin = false
  JointType = 0 (Fixed)
  LengthMax = 0
  LengthMin = 0
  Offset2 = pos=(0,0,0) rot=(0,0,-1;1.5708rad)
  Placement1 = pos=(9.5,-477,76.75) rot=(0,0,1;0rad)
  Placement2 = pos=(-9.5,-5.68e-14,85) rot=(-0.707107,0.707107,0;3.14159rad)
  Reference1 = -> Assembly [drawer_back.Edge7,drawer_back.Vertex6]
  Reference2 = -> Assembly [drawer_sides.Edge9,drawer_sides.Vertex5]
FEATURE [App::FeaturePython] Joint011  label="StarrerVerbund003"  # Assembly joint (typed FeaturePython)
  Activated = true
  AngleMax = 0
  AngleMin = 0
  Detach1 = false
  Detach2 = false
  Distance = 0
  Distance2 = 0
  EnableAngleMax = false
  EnableAngleMin = false
  EnableLengthMax = false
  EnableLengthMin = false
  JointType = 0 (Fixed)
  LengthMax = 0
  LengthMin = 0
  Placement1 = pos=(-9.5,0,85) rot=(0,1,0;3.14159rad)
  Placement2 = pos=(9.5,-477,85) rot=(0,0,1;0rad)
  Reference1 = -> Assembly [drawer_sides001.Edge9,drawer_sides001.Vertex5]
  Reference2 = -> Assembly [drawer_front.Edge4,drawer_front.Vertex4]
FEATURE [App::FeaturePython] Joint012  label="StarrerVerbund004"  # Assembly joint (typed FeaturePython)
  Activated = true
  AngleMax = 0
  AngleMin = 0
  Detach1 = false
  Detach2 = false
  Distance = 0
  Distance2 = 0
  EnableAngleMax = false
  EnableAngleMin = false
  EnableLengthMax = false
  EnableLengthMin = false
  JointType = 0 (Fixed)
  LengthMax = 0
  LengthMin = 0
  Placement1 = pos=(0,269.75,0) rot=(-0.707107,0,0.707107;3.14159rad)
  Placement2 = pos=(1.5,-238.5,-75) rot=(-0.57735,-0.57735,0.57735;4.18879rad)
  Reference1 = -> Assembly [drawer_bottom.Edge9,drawer_bottom.Edge9]
  Reference2 = -> Assembly [drawer_front.Edge17,drawer_front.Edge17]
FEATURE [Assembly::JointGroup] Joints
  Group = -> [GroundedJoint,Joint,Joint003,Joint004,Joint005,Joint006,Joint007,Joint009,Joint010,Joint011,Joint012]
FEATURE [Assembly::AssemblyObject] Assembly  label="wardrobe_drawer_jan"
  Group = -> [Joints,hettich_rail_550,hettich_rail_551,drawer_sides,drawer_sides001,drawer_back,drawer_bottom,drawer_front,GroundedJoint,Joint,Joint003,Joint004,Joint005,Joint006,Joint007,Joint009,Joint010,Joint011,Joint012]
  Origin = -> Origin
  Type = Assembly
